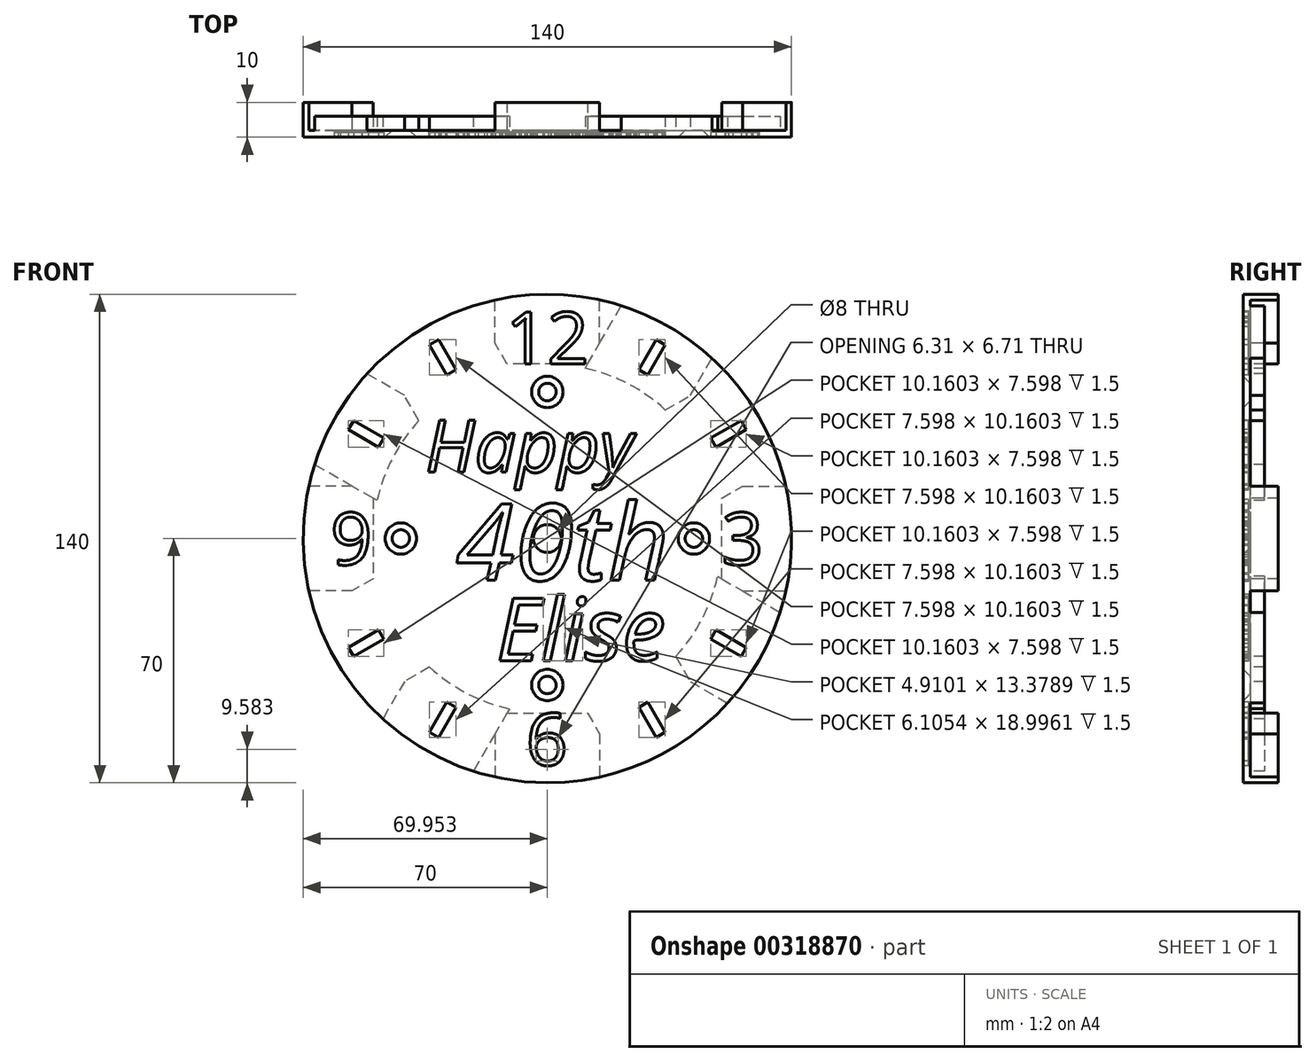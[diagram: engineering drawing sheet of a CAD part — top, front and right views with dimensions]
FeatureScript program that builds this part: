
annotation { "Feature Type Name" : "Feature", "Feature Type Description" : "" }
export const myFeature = defineFeature(function(context is Context, id is Id, definition is map)
    precondition{}
    {
        {
            var Q0;
            Q0=qCreatedBy(makeId("Front.planeOp"),FACE);
            var sketch = newSketch(context, id + "F0", { "sketchPlane" : qUnion([Q0])});
            skCircle(sketch, "E0", {"center": v(0, 0) * mm, "radius": 70 * mm});
            skCircle(sketch, "E1", {"center": v(0, 0) * mm, "radius": 50 * mm});
            skLineSegment(sketch, "E2", {"start": v(0, 50) * mm, "end": v(15, 50) * mm});
            skLineSegment(sketch, "E3.MirrorCS", {"start": v(0, 50) * mm, "end": v(-15, 50) * mm});
            skLineSegment(sketch, "E4", {"start": v(-15, 50) * mm, "end": v(-15, 87.34) * mm});
            skLineSegment(sketch, "E5.MirrorCS", {"start": v(15, 50) * mm, "end": v(15, 87.34) * mm});
            skCircle(sketch, "E6", {"center": v(0, 0) * mm, "radius": 30 * mm, "construction": true});
            skLineSegment(sketch, "E7", {"start": v(0, 0) * mm, "end": v(15, 25.98) * mm, "construction": true});
            skLineSegment(sketch, "E8", {"start": v(15, 25.98) * mm, "end": v(0, 0) * mm, "construction": true});
            skPoint(sketch, "E9.endSnap0", {"position": v(7.5, 13) * mm});
            skLineSegment(sketch, "E10", {"start": v(15, 25.98) * mm, "end": v(2, 33.48) * mm});
            skLineSegment(sketch, "E11.MirrorCS", {"start": v(15, 25.98) * mm, "end": v(28, 18.48) * mm});
            skLineSegment(sketch, "E12", {"start": v(2, 33.48) * mm, "end": v(34.2, 89.22) * mm});
            skLineSegment(sketch, "E13.MirrorCS", {"start": v(28, 18.48) * mm, "end": v(60.17, 74.22) * mm});
            skPoint(sketch, "E14.center", {"position": v(0, 10) * mm});
            skLineSegment(sketch, "E15", {"start": v(0, 0) * mm, "end": v(25.98, 15) * mm, "construction": true});
            skLineSegment(sketch, "E16", {"start": v(25.98, 15) * mm, "end": v(18.48, 28) * mm});
            skPoint(sketch, "E16.endSnap0", {"position": v(21.5, 22.23) * mm});
            skLineSegment(sketch, "E17", {"start": v(18.48, 28) * mm, "end": v(70.05, 57.76) * mm});
            skLineSegment(sketch, "E18.MirrorCS", {"start": v(25.98, 15) * mm, "end": v(33.48, 2) * mm});
            skLineSegment(sketch, "E19.MirrorCS", {"start": v(33.48, 2) * mm, "end": v(85.05, 31.78) * mm});
            skLineSegment(sketch, "E20.1.0", {"start": v(-50, -15) * mm, "end": v(-87.34, -15) * mm});
            skLineSegment(sketch, "E20.1.1", {"start": v(-50, 0) * mm, "end": v(-50, -15) * mm});
            skLineSegment(sketch, "E20.1.2", {"start": v(-50, 0) * mm, "end": v(-50, 15) * mm});
            skLineSegment(sketch, "E20.1.3", {"start": v(-50, 15) * mm, "end": v(-87.34, 15) * mm});
            skLineSegment(sketch, "E20.2.0", {"start": v(15, -50) * mm, "end": v(15, -87.34) * mm});
            skLineSegment(sketch, "E20.2.1", {"start": v(0, -50) * mm, "end": v(15, -50) * mm});
            skLineSegment(sketch, "E20.2.2", {"start": v(0, -50) * mm, "end": v(-15, -50) * mm});
            skLineSegment(sketch, "E20.2.3", {"start": v(-15, -50) * mm, "end": v(-15, -87.34) * mm});
            skLineSegment(sketch, "E20.3.0", {"start": v(50, 15) * mm, "end": v(87.34, 15) * mm});
            skLineSegment(sketch, "E20.3.1", {"start": v(50, 0) * mm, "end": v(50, 15) * mm});
            skLineSegment(sketch, "E20.3.2", {"start": v(50, 0) * mm, "end": v(50, -15) * mm});
            skLineSegment(sketch, "E20.3.3", {"start": v(50, -15) * mm, "end": v(87.34, -15) * mm});
            skLineSegment(sketch, "E21.1.0", {"start": v(-33.48, 2) * mm, "end": v(-89.22, 34.2) * mm});
            skLineSegment(sketch, "E21.1.1", {"start": v(-25.98, 15) * mm, "end": v(-33.48, 2) * mm});
            skLineSegment(sketch, "E21.1.2", {"start": v(-25.98, 15) * mm, "end": v(-18.48, 28) * mm});
            skLineSegment(sketch, "E21.1.3", {"start": v(-18.48, 28) * mm, "end": v(-74.22, 60.17) * mm});
            skLineSegment(sketch, "E21.2.0", {"start": v(-2, -33.48) * mm, "end": v(-34.2, -89.22) * mm});
            skLineSegment(sketch, "E21.2.1", {"start": v(-15, -25.98) * mm, "end": v(-2, -33.48) * mm});
            skLineSegment(sketch, "E21.2.2", {"start": v(-15, -25.98) * mm, "end": v(-28, -18.48) * mm});
            skLineSegment(sketch, "E21.2.3", {"start": v(-28, -18.48) * mm, "end": v(-60.17, -74.22) * mm});
            skLineSegment(sketch, "E21.3.0", {"start": v(33.48, -2) * mm, "end": v(89.22, -34.2) * mm});
            skLineSegment(sketch, "E21.3.1", {"start": v(25.98, -15) * mm, "end": v(33.48, -2) * mm});
            skLineSegment(sketch, "E21.3.2", {"start": v(25.98, -15) * mm, "end": v(18.48, -28) * mm});
            skLineSegment(sketch, "E21.3.3", {"start": v(18.48, -28) * mm, "end": v(74.22, -60.17) * mm});
            skLineSegment(sketch, "E22.1.0", {"start": v(-28, 18.48) * mm, "end": v(-57.76, 70.05) * mm});
            skLineSegment(sketch, "E22.1.1", {"start": v(-15, 25.98) * mm, "end": v(-28, 18.48) * mm});
            skLineSegment(sketch, "E22.1.2", {"start": v(-15, 25.98) * mm, "end": v(-2, 33.48) * mm});
            skLineSegment(sketch, "E22.1.3", {"start": v(-2, 33.48) * mm, "end": v(-31.78, 85.05) * mm});
            skLineSegment(sketch, "E22.2.0", {"start": v(-18.48, -28) * mm, "end": v(-70.05, -57.76) * mm});
            skLineSegment(sketch, "E22.2.1", {"start": v(-25.98, -15) * mm, "end": v(-18.48, -28) * mm});
            skLineSegment(sketch, "E22.2.2", {"start": v(-25.98, -15) * mm, "end": v(-33.48, -2) * mm});
            skLineSegment(sketch, "E22.2.3", {"start": v(-33.48, -2) * mm, "end": v(-85.05, -31.78) * mm});
            skLineSegment(sketch, "E22.3.0", {"start": v(28, -18.48) * mm, "end": v(57.76, -70.05) * mm});
            skLineSegment(sketch, "E22.3.1", {"start": v(15, -25.98) * mm, "end": v(28, -18.48) * mm});
            skLineSegment(sketch, "E22.3.2", {"start": v(15, -25.98) * mm, "end": v(2, -33.48) * mm});
            skLineSegment(sketch, "E22.3.3", {"start": v(2, -33.48) * mm, "end": v(31.78, -85.05) * mm});
            skCircle(sketch, "E23", {"center": v(0, 0) * mm, "radius": 4 * mm});
            skSolve(sketch);
        }
        {
            var Q0;
            {var subQ9=sQuery(id+"F0.wireOp",EDGE,"E10");Q0=makeQuery(id+"F0.imprint","IMPRINT",FACE,{"disambiguationData":[TD([[makeQuery(id+"F0.imprint","IMPRINT",EDGE,{"derivedFrom":subQ9}),1.0]])]});}
            var Q1;
            {var subQ0=sQuery(id+"F0.wireOp",EDGE,"E21.1.1");Q1=makeQuery(id+"F0.imprint","IMPRINT",FACE,{"disambiguationData":[TD([[makeQuery(id+"F0.imprint","IMPRINT",EDGE,{"derivedFrom":subQ0}),-1.0]])]});}
            var Q2;
            {var subQ6=sQuery(id+"F0.wireOp",EDGE,"E0");var subQ12=sQuery(id+"F0.wireOp",EDGE,"E21.1.3");var subQ13=makeQuery(id+"F0.imprint","INTERSECT",VERTEX,{"derivedFrom":[subQ6,subQ12]});Q2=makeQuery(id+"F0.imprint","IMPRINT",FACE,{"disambiguationData":[TD([[makeQuery(id+"F0.imprint","IMPRINT",EDGE,{"disambiguationData":[TD([[subQ13,-1.0]])],"derivedFrom":subQ6}),1.0]])]});}
            var Q3;
            {var subQ0=sQuery(id+"F0.wireOp",EDGE,"E21.1.0");var subQ1=sQuery(id+"F0.wireOp",EDGE,"E0");var subQ2=makeQuery(id+"F0.imprint","INTERSECT",VERTEX,{"derivedFrom":[subQ1,subQ0]});Q3=makeQuery(id+"F0.imprint","IMPRINT",FACE,{"disambiguationData":[TD([[makeQuery(id+"F0.imprint","IMPRINT",EDGE,{"disambiguationData":[TD([[subQ2,-1.0]])],"derivedFrom":subQ1}),1.0]])]});}
            var Q4;
            {var subQ1=sQuery(id+"F0.wireOp",EDGE,"E1");var subQ3=sQuery(id+"F0.wireOp",EDGE,"E21.1.0");var subQ4=makeQuery(id+"F0.imprint","INTERSECT",VERTEX,{"derivedFrom":[subQ1,subQ3]});Q4=makeQuery(id+"F0.imprint","IMPRINT",FACE,{"disambiguationData":[TD([[makeQuery(id+"F0.imprint","IMPRINT",EDGE,{"disambiguationData":[TD([[subQ4,-1.0]])],"derivedFrom":subQ3}),1.0]])]});}
            var Q5;
            {var subQ1=sQuery(id+"F0.wireOp",EDGE,"E1");var subQ3=sQuery(id+"F0.wireOp",EDGE,"E22.2.3");var subQ4=makeQuery(id+"F0.imprint","INTERSECT",VERTEX,{"derivedFrom":[subQ1,subQ3]});Q5=makeQuery(id+"F0.imprint","IMPRINT",FACE,{"disambiguationData":[TD([[makeQuery(id+"F0.imprint","IMPRINT",EDGE,{"disambiguationData":[TD([[subQ4,-1.0]])],"derivedFrom":subQ3}),-1.0]])]});}
            var Q6;
            {var subQ3=sQuery(id+"F0.wireOp",EDGE,"E22.2.3");var subQ6=sQuery(id+"F0.wireOp",EDGE,"E0");var subQ14=makeQuery(id+"F0.imprint","INTERSECT",VERTEX,{"derivedFrom":[subQ6,subQ3]});Q6=makeQuery(id+"F0.imprint","IMPRINT",FACE,{"disambiguationData":[TD([[makeQuery(id+"F0.imprint","IMPRINT",EDGE,{"disambiguationData":[TD([[subQ14,-1.0]])],"derivedFrom":subQ6}),1.0]])]});}
            var Q7;
            {var subQ0=sQuery(id+"F0.wireOp",EDGE,"E22.2.2");Q7=makeQuery(id+"F0.imprint","IMPRINT",FACE,{"disambiguationData":[TD([[makeQuery(id+"F0.imprint","IMPRINT",EDGE,{"derivedFrom":subQ0}),1.0]])]});}
            var Q8;
            {var subQ0=sQuery(id+"F0.wireOp",EDGE,"E20.1.0");var subQ1=sQuery(id+"F0.wireOp",EDGE,"E0");var subQ2=makeQuery(id+"F0.imprint","INTERSECT",VERTEX,{"derivedFrom":[subQ1,subQ0]});Q8=makeQuery(id+"F0.imprint","IMPRINT",FACE,{"disambiguationData":[TD([[makeQuery(id+"F0.imprint","IMPRINT",EDGE,{"disambiguationData":[TD([[subQ2,-1.0]])],"derivedFrom":subQ1}),1.0]])]});}
            var Q9;
            {var subQ0=sQuery(id+"F0.wireOp",EDGE,"E22.2.0");var subQ1=sQuery(id+"F0.wireOp",EDGE,"E0");var subQ2=makeQuery(id+"F0.imprint","INTERSECT",VERTEX,{"derivedFrom":[subQ1,subQ0]});Q9=makeQuery(id+"F0.imprint","IMPRINT",FACE,{"disambiguationData":[TD([[makeQuery(id+"F0.imprint","IMPRINT",EDGE,{"disambiguationData":[TD([[subQ2,-1.0]])],"derivedFrom":subQ1}),1.0]])]});}
            var Q10;
            {var subQ0=sQuery(id+"F0.wireOp",EDGE,"E21.2.0");var subQ1=sQuery(id+"F0.wireOp",EDGE,"E0");var subQ2=makeQuery(id+"F0.imprint","INTERSECT",VERTEX,{"derivedFrom":[subQ1,subQ0]});Q10=makeQuery(id+"F0.imprint","IMPRINT",FACE,{"disambiguationData":[TD([[makeQuery(id+"F0.imprint","IMPRINT",EDGE,{"disambiguationData":[TD([[subQ2,-1.0]])],"derivedFrom":subQ1}),1.0]])]});}
            var Q11;
            {var subQ0=sQuery(id+"F0.wireOp",EDGE,"E21.2.3");var subQ3=sQuery(id+"F0.wireOp",EDGE,"E1");var subQ4=makeQuery(id+"F0.imprint","INTERSECT",VERTEX,{"derivedFrom":[subQ3,subQ0]});Q11=makeQuery(id+"F0.imprint","IMPRINT",FACE,{"disambiguationData":[TD([[makeQuery(id+"F0.imprint","IMPRINT",EDGE,{"disambiguationData":[TD([[subQ4,-1.0]])],"derivedFrom":subQ3}),1.0]])]});}
            var Q12;
            {var subQ0=sQuery(id+"F0.wireOp",EDGE,"E21.2.1");Q12=makeQuery(id+"F0.imprint","IMPRINT",FACE,{"disambiguationData":[TD([[makeQuery(id+"F0.imprint","IMPRINT",EDGE,{"derivedFrom":subQ0}),-1.0]])]});}
            var Q13;
            {var subQ0=sQuery(id+"F0.wireOp",EDGE,"E21.2.3");var subQ1=sQuery(id+"F0.wireOp",EDGE,"E1");var subQ2=makeQuery(id+"F0.imprint","INTERSECT",VERTEX,{"derivedFrom":[subQ1,subQ0]});Q13=makeQuery(id+"F0.imprint","IMPRINT",FACE,{"disambiguationData":[TD([[makeQuery(id+"F0.imprint","IMPRINT",EDGE,{"disambiguationData":[TD([[subQ2,-1.0]])],"derivedFrom":subQ1}),-1.0]])]});}
            var Q14;
            {var subQ9=sQuery(id+"F0.wireOp",EDGE,"E21.2.3");var subQ10=sQuery(id+"F0.wireOp",EDGE,"E0");var subQ11=makeQuery(id+"F0.imprint","INTERSECT",VERTEX,{"derivedFrom":[subQ10,subQ9]});Q14=makeQuery(id+"F0.imprint","IMPRINT",FACE,{"disambiguationData":[TD([[makeQuery(id+"F0.imprint","IMPRINT",EDGE,{"disambiguationData":[TD([[subQ11,-1.0]])],"derivedFrom":subQ10}),1.0]])]});}
            var Q15;
            {var subQ1=sQuery(id+"F0.wireOp",EDGE,"E1");var subQ3=sQuery(id+"F0.wireOp",EDGE,"E21.2.0");var subQ4=makeQuery(id+"F0.imprint","INTERSECT",VERTEX,{"derivedFrom":[subQ1,subQ3]});Q15=makeQuery(id+"F0.imprint","IMPRINT",FACE,{"disambiguationData":[TD([[makeQuery(id+"F0.imprint","IMPRINT",EDGE,{"disambiguationData":[TD([[subQ4,-1.0]])],"derivedFrom":subQ3}),1.0]])]});}
            var Q16;
            {var subQ1=sQuery(id+"F0.wireOp",EDGE,"E1");var subQ3=sQuery(id+"F0.wireOp",EDGE,"E22.3.3");var subQ4=makeQuery(id+"F0.imprint","INTERSECT",VERTEX,{"derivedFrom":[subQ1,subQ3]});Q16=makeQuery(id+"F0.imprint","IMPRINT",FACE,{"disambiguationData":[TD([[makeQuery(id+"F0.imprint","IMPRINT",EDGE,{"disambiguationData":[TD([[subQ4,-1.0]])],"derivedFrom":subQ3}),-1.0]])]});}
            var Q17;
            {var subQ0=sQuery(id+"F0.wireOp",EDGE,"E20.2.0");var subQ1=sQuery(id+"F0.wireOp",EDGE,"E0");var subQ2=makeQuery(id+"F0.imprint","INTERSECT",VERTEX,{"derivedFrom":[subQ1,subQ0]});Q17=makeQuery(id+"F0.imprint","IMPRINT",FACE,{"disambiguationData":[TD([[makeQuery(id+"F0.imprint","IMPRINT",EDGE,{"disambiguationData":[TD([[subQ2,-1.0]])],"derivedFrom":subQ1}),1.0]])]});}
            var Q18;
            {var subQ0=sQuery(id+"F0.wireOp",EDGE,"E22.3.2");Q18=makeQuery(id+"F0.imprint","IMPRINT",FACE,{"disambiguationData":[TD([[makeQuery(id+"F0.imprint","IMPRINT",EDGE,{"derivedFrom":subQ0}),1.0]])]});}
            var Q19;
            {var subQ3=sQuery(id+"F0.wireOp",EDGE,"E22.3.3");var subQ12=sQuery(id+"F0.wireOp",EDGE,"E0");var subQ13=makeQuery(id+"F0.imprint","INTERSECT",VERTEX,{"derivedFrom":[subQ12,subQ3]});Q19=makeQuery(id+"F0.imprint","IMPRINT",FACE,{"disambiguationData":[TD([[makeQuery(id+"F0.imprint","IMPRINT",EDGE,{"disambiguationData":[TD([[subQ13,-1.0]])],"derivedFrom":subQ12}),1.0]])]});}
            var Q20;
            {var subQ0=sQuery(id+"F0.wireOp",EDGE,"E21.3.3");var subQ3=sQuery(id+"F0.wireOp",EDGE,"E1");var subQ4=makeQuery(id+"F0.imprint","INTERSECT",VERTEX,{"derivedFrom":[subQ3,subQ0]});Q20=makeQuery(id+"F0.imprint","IMPRINT",FACE,{"disambiguationData":[TD([[makeQuery(id+"F0.imprint","IMPRINT",EDGE,{"disambiguationData":[TD([[subQ4,-1.0]])],"derivedFrom":subQ3}),1.0]])]});}
            var Q21;
            {var subQ0=sQuery(id+"F0.wireOp",EDGE,"E21.3.1");Q21=makeQuery(id+"F0.imprint","IMPRINT",FACE,{"disambiguationData":[TD([[makeQuery(id+"F0.imprint","IMPRINT",EDGE,{"derivedFrom":subQ0}),-1.0]])]});}
            var Q22;
            {var subQ0=sQuery(id+"F0.wireOp",EDGE,"E21.3.3");var subQ1=sQuery(id+"F0.wireOp",EDGE,"E1");var subQ2=makeQuery(id+"F0.imprint","INTERSECT",VERTEX,{"derivedFrom":[subQ1,subQ0]});Q22=makeQuery(id+"F0.imprint","IMPRINT",FACE,{"disambiguationData":[TD([[makeQuery(id+"F0.imprint","IMPRINT",EDGE,{"disambiguationData":[TD([[subQ2,-1.0]])],"derivedFrom":subQ1}),-1.0]])]});}
            var Q23;
            {var subQ0=sQuery(id+"F0.wireOp",EDGE,"E22.3.0");var subQ1=sQuery(id+"F0.wireOp",EDGE,"E0");var subQ2=makeQuery(id+"F0.imprint","INTERSECT",VERTEX,{"derivedFrom":[subQ1,subQ0]});Q23=makeQuery(id+"F0.imprint","IMPRINT",FACE,{"disambiguationData":[TD([[makeQuery(id+"F0.imprint","IMPRINT",EDGE,{"disambiguationData":[TD([[subQ2,-1.0]])],"derivedFrom":subQ1}),1.0]])]});}
            var Q24;
            {var subQ10=sQuery(id+"F0.wireOp",EDGE,"E0");var subQ12=sQuery(id+"F0.wireOp",EDGE,"E21.3.3");var subQ13=makeQuery(id+"F0.imprint","INTERSECT",VERTEX,{"derivedFrom":[subQ10,subQ12]});Q24=makeQuery(id+"F0.imprint","IMPRINT",FACE,{"disambiguationData":[TD([[makeQuery(id+"F0.imprint","IMPRINT",EDGE,{"disambiguationData":[TD([[subQ13,-1.0]])],"derivedFrom":subQ10}),1.0]])]});}
            var Q25;
            {var subQ1=sQuery(id+"F0.wireOp",EDGE,"E1");var subQ3=sQuery(id+"F0.wireOp",EDGE,"E21.3.0");var subQ4=makeQuery(id+"F0.imprint","INTERSECT",VERTEX,{"derivedFrom":[subQ1,subQ3]});Q25=makeQuery(id+"F0.imprint","IMPRINT",FACE,{"disambiguationData":[TD([[makeQuery(id+"F0.imprint","IMPRINT",EDGE,{"disambiguationData":[TD([[subQ4,-1.0]])],"derivedFrom":subQ3}),1.0]])]});}
            var Q26;
            {var subQ1=sQuery(id+"F0.wireOp",EDGE,"E1");var subQ3=sQuery(id+"F0.wireOp",EDGE,"E19.MirrorCS");var subQ4=makeQuery(id+"F0.imprint","INTERSECT",VERTEX,{"derivedFrom":[subQ1,subQ3]});Q26=makeQuery(id+"F0.imprint","IMPRINT",FACE,{"disambiguationData":[TD([[makeQuery(id+"F0.imprint","IMPRINT",EDGE,{"disambiguationData":[TD([[subQ4,-1.0]])],"derivedFrom":subQ3}),-1.0]])]});}
            var Q27;
            {var subQ0=sQuery(id+"F0.wireOp",EDGE,"E18.MirrorCS");Q27=makeQuery(id+"F0.imprint","IMPRINT",FACE,{"disambiguationData":[TD([[makeQuery(id+"F0.imprint","IMPRINT",EDGE,{"derivedFrom":subQ0}),1.0]])]});}
            var Q28;
            {var subQ5=sQuery(id+"F0.wireOp",EDGE,"E19.MirrorCS");var subQ6=sQuery(id+"F0.wireOp",EDGE,"E0");var subQ7=makeQuery(id+"F0.imprint","INTERSECT",VERTEX,{"derivedFrom":[subQ6,subQ5]});Q28=makeQuery(id+"F0.imprint","IMPRINT",FACE,{"disambiguationData":[TD([[makeQuery(id+"F0.imprint","IMPRINT",EDGE,{"disambiguationData":[TD([[subQ7,-1.0]])],"derivedFrom":subQ6}),1.0]])]});}
            var Q29;
            {var subQ0=sQuery(id+"F0.wireOp",EDGE,"E19.MirrorCS");var subQ1=sQuery(id+"F0.wireOp",EDGE,"E0");var subQ2=makeQuery(id+"F0.imprint","INTERSECT",VERTEX,{"derivedFrom":[subQ1,subQ0]});Q29=makeQuery(id+"F0.imprint","IMPRINT",FACE,{"disambiguationData":[TD([[makeQuery(id+"F0.imprint","IMPRINT",EDGE,{"disambiguationData":[TD([[subQ2,1.0]])],"derivedFrom":subQ1}),1.0]])]});}
            var Q30;
            {var subQ5=sQuery(id+"F0.wireOp",EDGE,"E13.MirrorCS");var subQ7=sQuery(id+"F0.wireOp",EDGE,"E1");var subQ8=makeQuery(id+"F0.imprint","INTERSECT",VERTEX,{"derivedFrom":[subQ7,subQ5]});Q30=makeQuery(id+"F0.imprint","IMPRINT",FACE,{"disambiguationData":[TD([[makeQuery(id+"F0.imprint","IMPRINT",EDGE,{"disambiguationData":[TD([[subQ8,-1.0]])],"derivedFrom":subQ7}),1.0]])]});}
            var Q31;
            {var subQ1=sQuery(id+"F0.wireOp",EDGE,"E10");Q31=makeQuery(id+"F0.imprint","IMPRINT",FACE,{"disambiguationData":[TD([[makeQuery(id+"F0.imprint","IMPRINT",EDGE,{"derivedFrom":subQ1}),-1.0]])]});}
            var Q32;
            {var subQ0=sQuery(id+"F0.wireOp",EDGE,"E13.MirrorCS");var subQ1=sQuery(id+"F0.wireOp",EDGE,"E1");var subQ2=makeQuery(id+"F0.imprint","INTERSECT",VERTEX,{"derivedFrom":[subQ1,subQ0]});Q32=makeQuery(id+"F0.imprint","IMPRINT",FACE,{"disambiguationData":[TD([[makeQuery(id+"F0.imprint","IMPRINT",EDGE,{"disambiguationData":[TD([[subQ2,-1.0]])],"derivedFrom":subQ1}),-1.0]])]});}
            var Q33;
            {var subQ5=sQuery(id+"F0.wireOp",EDGE,"E13.MirrorCS");var subQ6=sQuery(id+"F0.wireOp",EDGE,"E0");var subQ7=makeQuery(id+"F0.imprint","INTERSECT",VERTEX,{"derivedFrom":[subQ6,subQ5]});Q33=makeQuery(id+"F0.imprint","IMPRINT",FACE,{"disambiguationData":[TD([[makeQuery(id+"F0.imprint","IMPRINT",EDGE,{"disambiguationData":[TD([[subQ7,-1.0]])],"derivedFrom":subQ6}),1.0]])]});}
            var Q34;
            {var subQ0=sQuery(id+"F0.wireOp",EDGE,"E17");var subQ1=sQuery(id+"F0.wireOp",EDGE,"E0");var subQ2=makeQuery(id+"F0.imprint","INTERSECT",VERTEX,{"derivedFrom":[subQ1,subQ0]});Q34=makeQuery(id+"F0.imprint","IMPRINT",FACE,{"disambiguationData":[TD([[makeQuery(id+"F0.imprint","IMPRINT",EDGE,{"disambiguationData":[TD([[subQ2,-1.0]])],"derivedFrom":subQ1}),1.0]])]});}
            var Q35;
            {var subQ0=sQuery(id+"F0.wireOp",EDGE,"E12");var subQ1=sQuery(id+"F0.wireOp",EDGE,"E0");var subQ2=makeQuery(id+"F0.imprint","INTERSECT",VERTEX,{"derivedFrom":[subQ1,subQ0]});Q35=makeQuery(id+"F0.imprint","IMPRINT",FACE,{"disambiguationData":[TD([[makeQuery(id+"F0.imprint","IMPRINT",EDGE,{"disambiguationData":[TD([[subQ2,-1.0]])],"derivedFrom":subQ1}),1.0]])]});}
            var Q36;
            {var subQ1=sQuery(id+"F0.wireOp",EDGE,"E1");var subQ3=sQuery(id+"F0.wireOp",EDGE,"E12");var subQ4=makeQuery(id+"F0.imprint","INTERSECT",VERTEX,{"derivedFrom":[subQ1,subQ3]});Q36=makeQuery(id+"F0.imprint","IMPRINT",FACE,{"disambiguationData":[TD([[makeQuery(id+"F0.imprint","IMPRINT",EDGE,{"disambiguationData":[TD([[subQ4,-1.0]])],"derivedFrom":subQ3}),1.0]])]});}
            var Q37;
            {var subQ1=sQuery(id+"F0.wireOp",EDGE,"E1");var subQ3=sQuery(id+"F0.wireOp",EDGE,"E22.1.3");var subQ4=makeQuery(id+"F0.imprint","INTERSECT",VERTEX,{"derivedFrom":[subQ1,subQ3]});Q37=makeQuery(id+"F0.imprint","IMPRINT",FACE,{"disambiguationData":[TD([[makeQuery(id+"F0.imprint","IMPRINT",EDGE,{"disambiguationData":[TD([[subQ4,-1.0]])],"derivedFrom":subQ3}),-1.0]])]});}
            var Q38;
            {var subQ0=sQuery(id+"F0.wireOp",EDGE,"E22.1.2");Q38=makeQuery(id+"F0.imprint","IMPRINT",FACE,{"disambiguationData":[TD([[makeQuery(id+"F0.imprint","IMPRINT",EDGE,{"derivedFrom":subQ0}),1.0]])]});}
            var Q39;
            {var subQ0=sQuery(id+"F0.wireOp",EDGE,"E21.1.3");var subQ3=sQuery(id+"F0.wireOp",EDGE,"E1");var subQ4=makeQuery(id+"F0.imprint","INTERSECT",VERTEX,{"derivedFrom":[subQ3,subQ0]});Q39=makeQuery(id+"F0.imprint","IMPRINT",FACE,{"disambiguationData":[TD([[makeQuery(id+"F0.imprint","IMPRINT",EDGE,{"disambiguationData":[TD([[subQ4,-1.0]])],"derivedFrom":subQ3}),1.0]])]});}
            var Q40;
            {var subQ0=sQuery(id+"F0.wireOp",EDGE,"E21.1.3");var subQ1=sQuery(id+"F0.wireOp",EDGE,"E1");var subQ2=makeQuery(id+"F0.imprint","INTERSECT",VERTEX,{"derivedFrom":[subQ1,subQ0]});Q40=makeQuery(id+"F0.imprint","IMPRINT",FACE,{"disambiguationData":[TD([[makeQuery(id+"F0.imprint","IMPRINT",EDGE,{"disambiguationData":[TD([[subQ2,-1.0]])],"derivedFrom":subQ1}),-1.0]])]});}
            var Q41;
            {var subQ0=sQuery(id+"F0.wireOp",EDGE,"E22.1.0");var subQ1=sQuery(id+"F0.wireOp",EDGE,"E0");var subQ2=makeQuery(id+"F0.imprint","INTERSECT",VERTEX,{"derivedFrom":[subQ1,subQ0]});Q41=makeQuery(id+"F0.imprint","IMPRINT",FACE,{"disambiguationData":[TD([[makeQuery(id+"F0.imprint","IMPRINT",EDGE,{"disambiguationData":[TD([[subQ2,-1.0]])],"derivedFrom":subQ1}),1.0]])]});}
            var Q42;
            {var subQ3=sQuery(id+"F0.wireOp",EDGE,"E22.1.3");var subQ10=sQuery(id+"F0.wireOp",EDGE,"E0");var subQ11=makeQuery(id+"F0.imprint","INTERSECT",VERTEX,{"derivedFrom":[subQ10,subQ3]});Q42=makeQuery(id+"F0.imprint","IMPRINT",FACE,{"disambiguationData":[TD([[makeQuery(id+"F0.imprint","IMPRINT",EDGE,{"disambiguationData":[TD([[subQ11,-1.0]])],"derivedFrom":subQ10}),1.0]])]});}
            var Q43;
            {var subQ0=sQuery(id+"F0.wireOp",EDGE,"E4");var subQ1=sQuery(id+"F0.wireOp",EDGE,"E0");var subQ2=makeQuery(id+"F0.imprint","INTERSECT",VERTEX,{"derivedFrom":[subQ1,subQ0]});Q43=makeQuery(id+"F0.imprint","IMPRINT",FACE,{"disambiguationData":[TD([[makeQuery(id+"F0.imprint","IMPRINT",EDGE,{"disambiguationData":[TD([[subQ2,-1.0]])],"derivedFrom":subQ1}),1.0]])]});}
            var Q44;
            {var subQ0=sQuery(id+"F0.wireOp",EDGE,"E21.3.0");var subQ1=sQuery(id+"F0.wireOp",EDGE,"E0");var subQ2=makeQuery(id+"F0.imprint","INTERSECT",VERTEX,{"derivedFrom":[subQ1,subQ0]});Q44=makeQuery(id+"F0.imprint","IMPRINT",FACE,{"disambiguationData":[TD([[makeQuery(id+"F0.imprint","IMPRINT",EDGE,{"disambiguationData":[TD([[subQ2,-1.0]])],"derivedFrom":subQ1}),1.0]])]});}
            var Q45;
            {var subQ0=sQuery(id+"F0.wireOp",EDGE,"E4");var subQ1=sQuery(id+"F0.wireOp",EDGE,"E3.MirrorCS");var subQ2=makeQuery(id+"F0.imprint","INTERSECT",VERTEX,{"derivedFrom":[subQ1,subQ0]});Q45=makeQuery(id+"F0.imprint","IMPRINT",FACE,{"disambiguationData":[TD([[makeQuery(id+"F0.imprint","IMPRINT",EDGE,{"disambiguationData":[TD([[subQ2,1.0]])],"derivedFrom":subQ1}),-1.0]])]});}
            var Q46;
            {var subQ7=sQuery(id+"F0.wireOp",EDGE,"E5.MirrorCS");var subQ11=sQuery(id+"F0.wireOp",EDGE,"E0");var subQ13=makeQuery(id+"F0.imprint","INTERSECT",VERTEX,{"derivedFrom":[subQ11,subQ7]});Q46=makeQuery(id+"F0.imprint","IMPRINT",FACE,{"disambiguationData":[TD([[makeQuery(id+"F0.imprint","IMPRINT",EDGE,{"disambiguationData":[TD([[subQ13,-1.0]])],"derivedFrom":subQ11}),1.0]])]});}
            var Q47;
            {var subQ0=sQuery(id+"F0.wireOp",EDGE,"E5.MirrorCS");var subQ1=sQuery(id+"F0.wireOp",EDGE,"E2");var subQ2=makeQuery(id+"F0.imprint","INTERSECT",VERTEX,{"derivedFrom":[subQ1,subQ0]});Q47=makeQuery(id+"F0.imprint","IMPRINT",FACE,{"disambiguationData":[TD([[makeQuery(id+"F0.imprint","IMPRINT",EDGE,{"disambiguationData":[TD([[subQ2,1.0]])],"derivedFrom":subQ1}),1.0]])]});}
            var Q48;
            {var subQ6=sQuery(id+"F0.wireOp",EDGE,"E0");var subQ11=sQuery(id+"F0.wireOp",EDGE,"E20.1.3");var subQ13=makeQuery(id+"F0.imprint","INTERSECT",VERTEX,{"derivedFrom":[subQ6,subQ11]});Q48=makeQuery(id+"F0.imprint","IMPRINT",FACE,{"disambiguationData":[TD([[makeQuery(id+"F0.imprint","IMPRINT",EDGE,{"disambiguationData":[TD([[subQ13,-1.0]])],"derivedFrom":subQ6}),1.0]])]});}
            var Q49;
            {var subQ0=sQuery(id+"F0.wireOp",EDGE,"E20.1.3");var subQ1=sQuery(id+"F0.wireOp",EDGE,"E20.1.2");var subQ2=makeQuery(id+"F0.imprint","INTERSECT",VERTEX,{"derivedFrom":[subQ1,subQ0]});Q49=makeQuery(id+"F0.imprint","IMPRINT",FACE,{"disambiguationData":[TD([[makeQuery(id+"F0.imprint","IMPRINT",EDGE,{"disambiguationData":[TD([[subQ2,1.0]])],"derivedFrom":subQ1}),1.0]])]});}
            var Q50;
            {var subQ0=sQuery(id+"F0.wireOp",EDGE,"E20.1.1");var subQ1=sQuery(id+"F0.wireOp",EDGE,"E20.1.0");var subQ2=makeQuery(id+"F0.imprint","INTERSECT",VERTEX,{"derivedFrom":[subQ1,subQ0]});Q50=makeQuery(id+"F0.imprint","IMPRINT",FACE,{"disambiguationData":[TD([[makeQuery(id+"F0.imprint","IMPRINT",EDGE,{"disambiguationData":[TD([[subQ2,-1.0]])],"derivedFrom":subQ1}),-1.0]])]});}
            var Q51;
            {var subQ6=sQuery(id+"F0.wireOp",EDGE,"E0");var subQ11=sQuery(id+"F0.wireOp",EDGE,"E20.2.3");var subQ12=makeQuery(id+"F0.imprint","INTERSECT",VERTEX,{"derivedFrom":[subQ6,subQ11]});Q51=makeQuery(id+"F0.imprint","IMPRINT",FACE,{"disambiguationData":[TD([[makeQuery(id+"F0.imprint","IMPRINT",EDGE,{"disambiguationData":[TD([[subQ12,-1.0]])],"derivedFrom":subQ6}),1.0]])]});}
            var Q52;
            {var subQ0=sQuery(id+"F0.wireOp",EDGE,"E20.2.3");var subQ1=sQuery(id+"F0.wireOp",EDGE,"E20.2.2");var subQ2=makeQuery(id+"F0.imprint","INTERSECT",VERTEX,{"derivedFrom":[subQ1,subQ0]});Q52=makeQuery(id+"F0.imprint","IMPRINT",FACE,{"disambiguationData":[TD([[makeQuery(id+"F0.imprint","IMPRINT",EDGE,{"disambiguationData":[TD([[subQ2,1.0]])],"derivedFrom":subQ1}),1.0]])]});}
            var Q53;
            {var subQ0=sQuery(id+"F0.wireOp",EDGE,"E20.2.1");var subQ1=sQuery(id+"F0.wireOp",EDGE,"E20.2.0");var subQ2=makeQuery(id+"F0.imprint","INTERSECT",VERTEX,{"derivedFrom":[subQ1,subQ0]});Q53=makeQuery(id+"F0.imprint","IMPRINT",FACE,{"disambiguationData":[TD([[makeQuery(id+"F0.imprint","IMPRINT",EDGE,{"disambiguationData":[TD([[subQ2,-1.0]])],"derivedFrom":subQ1}),-1.0]])]});}
            var Q54;
            {var subQ0=sQuery(id+"F0.wireOp",EDGE,"E20.3.3");var subQ1=sQuery(id+"F0.wireOp",EDGE,"E20.3.2");var subQ2=makeQuery(id+"F0.imprint","INTERSECT",VERTEX,{"derivedFrom":[subQ1,subQ0]});Q54=makeQuery(id+"F0.imprint","IMPRINT",FACE,{"disambiguationData":[TD([[makeQuery(id+"F0.imprint","IMPRINT",EDGE,{"disambiguationData":[TD([[subQ2,1.0]])],"derivedFrom":subQ1}),1.0]])]});}
            var Q55;
            {var subQ0=sQuery(id+"F0.wireOp",EDGE,"E20.3.0");var subQ1=sQuery(id+"F0.wireOp",EDGE,"E0");var subQ2=makeQuery(id+"F0.imprint","INTERSECT",VERTEX,{"derivedFrom":[subQ1,subQ0]});Q55=makeQuery(id+"F0.imprint","IMPRINT",FACE,{"disambiguationData":[TD([[makeQuery(id+"F0.imprint","IMPRINT",EDGE,{"disambiguationData":[TD([[subQ2,1.0]])],"derivedFrom":subQ1}),1.0]])]});}
            var Q56;
            {var subQ0=sQuery(id+"F0.wireOp",EDGE,"E20.3.1");var subQ1=sQuery(id+"F0.wireOp",EDGE,"E19.MirrorCS");var subQ2=makeQuery(id+"F0.imprint","INTERSECT",VERTEX,{"derivedFrom":[subQ1,subQ0]});Q56=makeQuery(id+"F0.imprint","IMPRINT",FACE,{"disambiguationData":[TD([[makeQuery(id+"F0.imprint","IMPRINT",EDGE,{"disambiguationData":[TD([[subQ2,-1.0]])],"derivedFrom":subQ1}),1.0]])]});}
            extrude(context, id + "F1", {"entities" : qUnion([Q0, Q1, Q2, Q3, Q4, Q5, Q6, Q7, Q8, Q9, Q10, Q11, Q12, Q13, Q14, Q15, Q16, Q17, Q18, Q19, Q20, Q21, Q22, Q23, Q24, Q25, Q26, Q27, Q28, Q29, Q30, Q31, Q32, Q33, Q34, Q35, Q36, Q37, Q38, Q39, Q40, Q41, Q42, Q43, Q44, Q45, Q46, Q47, Q48, Q49, Q50, Q51, Q52, Q53, Q54, Q55, Q56]), "depth" : 8 * mm});
        }
        {
            var Q0;
            {var subQ0=sQuery(id+"F0.wireOp",EDGE,"E19.MirrorCS");var subQ1=sQuery(id+"F0.wireOp",EDGE,"E0");var subQ2=makeQuery(id+"F0.imprint","INTERSECT",VERTEX,{"derivedFrom":[subQ1,subQ0]});Q0=makeQuery(id+"F0.imprint","IMPRINT",FACE,{"disambiguationData":[TD([[makeQuery(id+"F0.imprint","IMPRINT",EDGE,{"disambiguationData":[TD([[subQ2,1.0]])],"derivedFrom":subQ1}),1.0]])]});}
            var Q1;
            {var subQ0=sQuery(id+"F0.wireOp",EDGE,"E20.3.0");var subQ1=sQuery(id+"F0.wireOp",EDGE,"E0");var subQ2=makeQuery(id+"F0.imprint","INTERSECT",VERTEX,{"derivedFrom":[subQ1,subQ0]});Q1=makeQuery(id+"F0.imprint","IMPRINT",FACE,{"disambiguationData":[TD([[makeQuery(id+"F0.imprint","IMPRINT",EDGE,{"disambiguationData":[TD([[subQ2,1.0]])],"derivedFrom":subQ1}),1.0]])]});}
            var Q2;
            {var subQ9=sQuery(id+"F0.wireOp",EDGE,"E10");Q2=makeQuery(id+"F0.imprint","IMPRINT",FACE,{"disambiguationData":[TD([[makeQuery(id+"F0.imprint","IMPRINT",EDGE,{"derivedFrom":subQ9}),1.0]])]});}
            var Q3;
            {var subQ1=sQuery(id+"F0.wireOp",EDGE,"E1");var subQ3=sQuery(id+"F0.wireOp",EDGE,"E19.MirrorCS");var subQ4=makeQuery(id+"F0.imprint","INTERSECT",VERTEX,{"derivedFrom":[subQ1,subQ3]});Q3=makeQuery(id+"F0.imprint","IMPRINT",FACE,{"disambiguationData":[TD([[makeQuery(id+"F0.imprint","IMPRINT",EDGE,{"disambiguationData":[TD([[subQ4,-1.0]])],"derivedFrom":subQ3}),-1.0]])]});}
            var Q4;
            {var subQ1=sQuery(id+"F0.wireOp",EDGE,"E1");var subQ3=sQuery(id+"F0.wireOp",EDGE,"E21.3.0");var subQ4=makeQuery(id+"F0.imprint","INTERSECT",VERTEX,{"derivedFrom":[subQ1,subQ3]});Q4=makeQuery(id+"F0.imprint","IMPRINT",FACE,{"disambiguationData":[TD([[makeQuery(id+"F0.imprint","IMPRINT",EDGE,{"disambiguationData":[TD([[subQ4,-1.0]])],"derivedFrom":subQ3}),1.0]])]});}
            var Q5;
            {var subQ1=sQuery(id+"F0.wireOp",EDGE,"E1");var subQ3=sQuery(id+"F0.wireOp",EDGE,"E12");var subQ4=makeQuery(id+"F0.imprint","INTERSECT",VERTEX,{"derivedFrom":[subQ1,subQ3]});Q5=makeQuery(id+"F0.imprint","IMPRINT",FACE,{"disambiguationData":[TD([[makeQuery(id+"F0.imprint","IMPRINT",EDGE,{"disambiguationData":[TD([[subQ4,-1.0]])],"derivedFrom":subQ3}),1.0]])]});}
            var Q6;
            {var subQ1=sQuery(id+"F0.wireOp",EDGE,"E1");var subQ3=sQuery(id+"F0.wireOp",EDGE,"E22.1.3");var subQ4=makeQuery(id+"F0.imprint","INTERSECT",VERTEX,{"derivedFrom":[subQ1,subQ3]});Q6=makeQuery(id+"F0.imprint","IMPRINT",FACE,{"disambiguationData":[TD([[makeQuery(id+"F0.imprint","IMPRINT",EDGE,{"disambiguationData":[TD([[subQ4,-1.0]])],"derivedFrom":subQ3}),-1.0]])]});}
            var Q7;
            {var subQ7=sQuery(id+"F0.wireOp",EDGE,"E5.MirrorCS");var subQ11=sQuery(id+"F0.wireOp",EDGE,"E0");var subQ13=makeQuery(id+"F0.imprint","INTERSECT",VERTEX,{"derivedFrom":[subQ11,subQ7]});Q7=makeQuery(id+"F0.imprint","IMPRINT",FACE,{"disambiguationData":[TD([[makeQuery(id+"F0.imprint","IMPRINT",EDGE,{"disambiguationData":[TD([[subQ13,-1.0]])],"derivedFrom":subQ11}),1.0]])]});}
            var Q8;
            {var subQ0=sQuery(id+"F0.wireOp",EDGE,"E12");var subQ1=sQuery(id+"F0.wireOp",EDGE,"E0");var subQ2=makeQuery(id+"F0.imprint","INTERSECT",VERTEX,{"derivedFrom":[subQ1,subQ0]});Q8=makeQuery(id+"F0.imprint","IMPRINT",FACE,{"disambiguationData":[TD([[makeQuery(id+"F0.imprint","IMPRINT",EDGE,{"disambiguationData":[TD([[subQ2,-1.0]])],"derivedFrom":subQ1}),1.0]])]});}
            var Q9;
            {var subQ0=sQuery(id+"F0.wireOp",EDGE,"E17");var subQ1=sQuery(id+"F0.wireOp",EDGE,"E0");var subQ2=makeQuery(id+"F0.imprint","INTERSECT",VERTEX,{"derivedFrom":[subQ1,subQ0]});Q9=makeQuery(id+"F0.imprint","IMPRINT",FACE,{"disambiguationData":[TD([[makeQuery(id+"F0.imprint","IMPRINT",EDGE,{"disambiguationData":[TD([[subQ2,-1.0]])],"derivedFrom":subQ1}),1.0]])]});}
            var Q10;
            {var subQ0=sQuery(id+"F0.wireOp",EDGE,"E4");var subQ1=sQuery(id+"F0.wireOp",EDGE,"E0");var subQ2=makeQuery(id+"F0.imprint","INTERSECT",VERTEX,{"derivedFrom":[subQ1,subQ0]});Q10=makeQuery(id+"F0.imprint","IMPRINT",FACE,{"disambiguationData":[TD([[makeQuery(id+"F0.imprint","IMPRINT",EDGE,{"disambiguationData":[TD([[subQ2,-1.0]])],"derivedFrom":subQ1}),1.0]])]});}
            var Q11;
            {var subQ0=sQuery(id+"F0.wireOp",EDGE,"E22.1.0");var subQ1=sQuery(id+"F0.wireOp",EDGE,"E0");var subQ2=makeQuery(id+"F0.imprint","INTERSECT",VERTEX,{"derivedFrom":[subQ1,subQ0]});Q11=makeQuery(id+"F0.imprint","IMPRINT",FACE,{"disambiguationData":[TD([[makeQuery(id+"F0.imprint","IMPRINT",EDGE,{"disambiguationData":[TD([[subQ2,-1.0]])],"derivedFrom":subQ1}),1.0]])]});}
            var Q12;
            {var subQ0=sQuery(id+"F0.wireOp",EDGE,"E21.1.0");var subQ1=sQuery(id+"F0.wireOp",EDGE,"E0");var subQ2=makeQuery(id+"F0.imprint","INTERSECT",VERTEX,{"derivedFrom":[subQ1,subQ0]});Q12=makeQuery(id+"F0.imprint","IMPRINT",FACE,{"disambiguationData":[TD([[makeQuery(id+"F0.imprint","IMPRINT",EDGE,{"disambiguationData":[TD([[subQ2,-1.0]])],"derivedFrom":subQ1}),1.0]])]});}
            var Q13;
            {var subQ1=sQuery(id+"F0.wireOp",EDGE,"E1");var subQ3=sQuery(id+"F0.wireOp",EDGE,"E21.1.0");var subQ4=makeQuery(id+"F0.imprint","INTERSECT",VERTEX,{"derivedFrom":[subQ1,subQ3]});Q13=makeQuery(id+"F0.imprint","IMPRINT",FACE,{"disambiguationData":[TD([[makeQuery(id+"F0.imprint","IMPRINT",EDGE,{"disambiguationData":[TD([[subQ4,-1.0]])],"derivedFrom":subQ3}),1.0]])]});}
            var Q14;
            {var subQ1=sQuery(id+"F0.wireOp",EDGE,"E1");var subQ3=sQuery(id+"F0.wireOp",EDGE,"E22.2.3");var subQ4=makeQuery(id+"F0.imprint","INTERSECT",VERTEX,{"derivedFrom":[subQ1,subQ3]});Q14=makeQuery(id+"F0.imprint","IMPRINT",FACE,{"disambiguationData":[TD([[makeQuery(id+"F0.imprint","IMPRINT",EDGE,{"disambiguationData":[TD([[subQ4,-1.0]])],"derivedFrom":subQ3}),-1.0]])]});}
            var Q15;
            {var subQ6=sQuery(id+"F0.wireOp",EDGE,"E0");var subQ11=sQuery(id+"F0.wireOp",EDGE,"E20.1.3");var subQ13=makeQuery(id+"F0.imprint","INTERSECT",VERTEX,{"derivedFrom":[subQ6,subQ11]});Q15=makeQuery(id+"F0.imprint","IMPRINT",FACE,{"disambiguationData":[TD([[makeQuery(id+"F0.imprint","IMPRINT",EDGE,{"disambiguationData":[TD([[subQ13,-1.0]])],"derivedFrom":subQ6}),1.0]])]});}
            var Q16;
            {var subQ0=sQuery(id+"F0.wireOp",EDGE,"E20.1.0");var subQ1=sQuery(id+"F0.wireOp",EDGE,"E0");var subQ2=makeQuery(id+"F0.imprint","INTERSECT",VERTEX,{"derivedFrom":[subQ1,subQ0]});Q16=makeQuery(id+"F0.imprint","IMPRINT",FACE,{"disambiguationData":[TD([[makeQuery(id+"F0.imprint","IMPRINT",EDGE,{"disambiguationData":[TD([[subQ2,-1.0]])],"derivedFrom":subQ1}),1.0]])]});}
            var Q17;
            {var subQ0=sQuery(id+"F0.wireOp",EDGE,"E21.3.0");var subQ1=sQuery(id+"F0.wireOp",EDGE,"E0");var subQ2=makeQuery(id+"F0.imprint","INTERSECT",VERTEX,{"derivedFrom":[subQ1,subQ0]});Q17=makeQuery(id+"F0.imprint","IMPRINT",FACE,{"disambiguationData":[TD([[makeQuery(id+"F0.imprint","IMPRINT",EDGE,{"disambiguationData":[TD([[subQ2,-1.0]])],"derivedFrom":subQ1}),1.0]])]});}
            var Q18;
            {var subQ0=sQuery(id+"F0.wireOp",EDGE,"E22.3.0");var subQ1=sQuery(id+"F0.wireOp",EDGE,"E0");var subQ2=makeQuery(id+"F0.imprint","INTERSECT",VERTEX,{"derivedFrom":[subQ1,subQ0]});Q18=makeQuery(id+"F0.imprint","IMPRINT",FACE,{"disambiguationData":[TD([[makeQuery(id+"F0.imprint","IMPRINT",EDGE,{"disambiguationData":[TD([[subQ2,-1.0]])],"derivedFrom":subQ1}),1.0]])]});}
            var Q19;
            {var subQ0=sQuery(id+"F0.wireOp",EDGE,"E20.2.0");var subQ1=sQuery(id+"F0.wireOp",EDGE,"E0");var subQ2=makeQuery(id+"F0.imprint","INTERSECT",VERTEX,{"derivedFrom":[subQ1,subQ0]});Q19=makeQuery(id+"F0.imprint","IMPRINT",FACE,{"disambiguationData":[TD([[makeQuery(id+"F0.imprint","IMPRINT",EDGE,{"disambiguationData":[TD([[subQ2,-1.0]])],"derivedFrom":subQ1}),1.0]])]});}
            var Q20;
            {var subQ6=sQuery(id+"F0.wireOp",EDGE,"E0");var subQ11=sQuery(id+"F0.wireOp",EDGE,"E20.2.3");var subQ12=makeQuery(id+"F0.imprint","INTERSECT",VERTEX,{"derivedFrom":[subQ6,subQ11]});Q20=makeQuery(id+"F0.imprint","IMPRINT",FACE,{"disambiguationData":[TD([[makeQuery(id+"F0.imprint","IMPRINT",EDGE,{"disambiguationData":[TD([[subQ12,-1.0]])],"derivedFrom":subQ6}),1.0]])]});}
            var Q21;
            {var subQ1=sQuery(id+"F0.wireOp",EDGE,"E1");var subQ3=sQuery(id+"F0.wireOp",EDGE,"E22.3.3");var subQ4=makeQuery(id+"F0.imprint","INTERSECT",VERTEX,{"derivedFrom":[subQ1,subQ3]});Q21=makeQuery(id+"F0.imprint","IMPRINT",FACE,{"disambiguationData":[TD([[makeQuery(id+"F0.imprint","IMPRINT",EDGE,{"disambiguationData":[TD([[subQ4,-1.0]])],"derivedFrom":subQ3}),-1.0]])]});}
            var Q22;
            {var subQ1=sQuery(id+"F0.wireOp",EDGE,"E1");var subQ3=sQuery(id+"F0.wireOp",EDGE,"E21.2.0");var subQ4=makeQuery(id+"F0.imprint","INTERSECT",VERTEX,{"derivedFrom":[subQ1,subQ3]});Q22=makeQuery(id+"F0.imprint","IMPRINT",FACE,{"disambiguationData":[TD([[makeQuery(id+"F0.imprint","IMPRINT",EDGE,{"disambiguationData":[TD([[subQ4,-1.0]])],"derivedFrom":subQ3}),1.0]])]});}
            var Q23;
            {var subQ0=sQuery(id+"F0.wireOp",EDGE,"E21.2.0");var subQ1=sQuery(id+"F0.wireOp",EDGE,"E0");var subQ2=makeQuery(id+"F0.imprint","INTERSECT",VERTEX,{"derivedFrom":[subQ1,subQ0]});Q23=makeQuery(id+"F0.imprint","IMPRINT",FACE,{"disambiguationData":[TD([[makeQuery(id+"F0.imprint","IMPRINT",EDGE,{"disambiguationData":[TD([[subQ2,-1.0]])],"derivedFrom":subQ1}),1.0]])]});}
            var Q24;
            {var subQ0=sQuery(id+"F0.wireOp",EDGE,"E22.2.0");var subQ1=sQuery(id+"F0.wireOp",EDGE,"E0");var subQ2=makeQuery(id+"F0.imprint","INTERSECT",VERTEX,{"derivedFrom":[subQ1,subQ0]});Q24=makeQuery(id+"F0.imprint","IMPRINT",FACE,{"disambiguationData":[TD([[makeQuery(id+"F0.imprint","IMPRINT",EDGE,{"disambiguationData":[TD([[subQ2,-1.0]])],"derivedFrom":subQ1}),1.0]])]});}
            extrude(context, id + "F2", {"entities" : qUnion([Q0, Q1, Q2, Q3, Q4, Q5, Q6, Q7, Q8, Q9, Q10, Q11, Q12, Q13, Q14, Q15, Q16, Q17, Q18, Q19, Q20, Q21, Q22, Q23, Q24]), "operationType" : NewBodyOperationType.ADD, "oppositeDirection" : true, "depth" : 8 * mm});
        }
        {
            var Q0;
            {var subQ5=sQuery(id+"F0.wireOp",EDGE,"E13.MirrorCS");var subQ6=sQuery(id+"F0.wireOp",EDGE,"E0");var subQ7=makeQuery(id+"F0.imprint","INTERSECT",VERTEX,{"derivedFrom":[subQ6,subQ5]});Q0=makeQuery(id+"F0.imprint","IMPRINT",FACE,{"disambiguationData":[TD([[makeQuery(id+"F0.imprint","IMPRINT",EDGE,{"disambiguationData":[TD([[subQ7,-1.0]])],"derivedFrom":subQ6}),1.0]])]});}
            var Q1;
            {var subQ0=sQuery(id+"F0.wireOp",EDGE,"E5.MirrorCS");var subQ1=sQuery(id+"F0.wireOp",EDGE,"E2");var subQ2=makeQuery(id+"F0.imprint","INTERSECT",VERTEX,{"derivedFrom":[subQ1,subQ0]});Q1=makeQuery(id+"F0.imprint","IMPRINT",FACE,{"disambiguationData":[TD([[makeQuery(id+"F0.imprint","IMPRINT",EDGE,{"disambiguationData":[TD([[subQ2,1.0]])],"derivedFrom":subQ1}),1.0]])]});}
            var Q2;
            {var subQ1=sQuery(id+"F0.wireOp",EDGE,"E10");Q2=makeQuery(id+"F0.imprint","IMPRINT",FACE,{"disambiguationData":[TD([[makeQuery(id+"F0.imprint","IMPRINT",EDGE,{"derivedFrom":subQ1}),-1.0]])]});}
            var Q3;
            {var subQ0=sQuery(id+"F0.wireOp",EDGE,"E20.1.3");var subQ1=sQuery(id+"F0.wireOp",EDGE,"E20.1.2");var subQ2=makeQuery(id+"F0.imprint","INTERSECT",VERTEX,{"derivedFrom":[subQ1,subQ0]});Q3=makeQuery(id+"F0.imprint","IMPRINT",FACE,{"disambiguationData":[TD([[makeQuery(id+"F0.imprint","IMPRINT",EDGE,{"disambiguationData":[TD([[subQ2,1.0]])],"derivedFrom":subQ1}),1.0]])]});}
            var Q4;
            {var subQ0=sQuery(id+"F0.wireOp",EDGE,"E21.1.1");Q4=makeQuery(id+"F0.imprint","IMPRINT",FACE,{"disambiguationData":[TD([[makeQuery(id+"F0.imprint","IMPRINT",EDGE,{"derivedFrom":subQ0}),-1.0]])]});}
            var Q5;
            {var subQ6=sQuery(id+"F0.wireOp",EDGE,"E0");var subQ12=sQuery(id+"F0.wireOp",EDGE,"E21.1.3");var subQ13=makeQuery(id+"F0.imprint","INTERSECT",VERTEX,{"derivedFrom":[subQ6,subQ12]});Q5=makeQuery(id+"F0.imprint","IMPRINT",FACE,{"disambiguationData":[TD([[makeQuery(id+"F0.imprint","IMPRINT",EDGE,{"disambiguationData":[TD([[subQ13,-1.0]])],"derivedFrom":subQ6}),1.0]])]});}
            var Q6;
            {var subQ0=sQuery(id+"F0.wireOp",EDGE,"E20.2.3");var subQ1=sQuery(id+"F0.wireOp",EDGE,"E20.2.2");var subQ2=makeQuery(id+"F0.imprint","INTERSECT",VERTEX,{"derivedFrom":[subQ1,subQ0]});Q6=makeQuery(id+"F0.imprint","IMPRINT",FACE,{"disambiguationData":[TD([[makeQuery(id+"F0.imprint","IMPRINT",EDGE,{"disambiguationData":[TD([[subQ2,1.0]])],"derivedFrom":subQ1}),1.0]])]});}
            var Q7;
            {var subQ0=sQuery(id+"F0.wireOp",EDGE,"E21.2.1");Q7=makeQuery(id+"F0.imprint","IMPRINT",FACE,{"disambiguationData":[TD([[makeQuery(id+"F0.imprint","IMPRINT",EDGE,{"derivedFrom":subQ0}),-1.0]])]});}
            var Q8;
            {var subQ9=sQuery(id+"F0.wireOp",EDGE,"E21.2.3");var subQ10=sQuery(id+"F0.wireOp",EDGE,"E0");var subQ11=makeQuery(id+"F0.imprint","INTERSECT",VERTEX,{"derivedFrom":[subQ10,subQ9]});Q8=makeQuery(id+"F0.imprint","IMPRINT",FACE,{"disambiguationData":[TD([[makeQuery(id+"F0.imprint","IMPRINT",EDGE,{"disambiguationData":[TD([[subQ11,-1.0]])],"derivedFrom":subQ10}),1.0]])]});}
            var Q9;
            {var subQ10=sQuery(id+"F0.wireOp",EDGE,"E0");var subQ12=sQuery(id+"F0.wireOp",EDGE,"E21.3.3");var subQ13=makeQuery(id+"F0.imprint","INTERSECT",VERTEX,{"derivedFrom":[subQ10,subQ12]});Q9=makeQuery(id+"F0.imprint","IMPRINT",FACE,{"disambiguationData":[TD([[makeQuery(id+"F0.imprint","IMPRINT",EDGE,{"disambiguationData":[TD([[subQ13,-1.0]])],"derivedFrom":subQ10}),1.0]])]});}
            var Q10;
            {var subQ0=sQuery(id+"F0.wireOp",EDGE,"E21.3.1");Q10=makeQuery(id+"F0.imprint","IMPRINT",FACE,{"disambiguationData":[TD([[makeQuery(id+"F0.imprint","IMPRINT",EDGE,{"derivedFrom":subQ0}),-1.0]])]});}
            var Q11;
            {var subQ0=sQuery(id+"F0.wireOp",EDGE,"E20.3.3");var subQ1=sQuery(id+"F0.wireOp",EDGE,"E20.3.2");var subQ2=makeQuery(id+"F0.imprint","INTERSECT",VERTEX,{"derivedFrom":[subQ1,subQ0]});Q11=makeQuery(id+"F0.imprint","IMPRINT",FACE,{"disambiguationData":[TD([[makeQuery(id+"F0.imprint","IMPRINT",EDGE,{"disambiguationData":[TD([[subQ2,1.0]])],"derivedFrom":subQ1}),1.0]])]});}
            extrude(context, id + "F3", {"entities" : qUnion([Q0, Q1, Q2, Q3, Q4, Q5, Q6, Q7, Q8, Q9, Q10, Q11]), "operationType" : NewBodyOperationType.ADD, "oppositeDirection" : true, "depth" : 4 * mm});
        }
        {
            var Q0;
            {var subQ7=sQuery(id+"F0.wireOp",EDGE,"E5.MirrorCS");var subQ11=sQuery(id+"F0.wireOp",EDGE,"E0");var subQ13=makeQuery(id+"F0.imprint","INTERSECT",VERTEX,{"derivedFrom":[subQ11,subQ7]});Q0=makeQuery(id+"F0.imprint","IMPRINT",FACE,{"disambiguationData":[TD([[makeQuery(id+"F0.imprint","IMPRINT",EDGE,{"disambiguationData":[TD([[subQ13,-1.0]])],"derivedFrom":subQ11}),1.0]])]});}
            var Q1;
            {var subQ0=sQuery(id+"F0.wireOp",EDGE,"E4");var subQ1=sQuery(id+"F0.wireOp",EDGE,"E3.MirrorCS");var subQ2=makeQuery(id+"F0.imprint","INTERSECT",VERTEX,{"derivedFrom":[subQ1,subQ0]});Q1=makeQuery(id+"F0.imprint","IMPRINT",FACE,{"disambiguationData":[TD([[makeQuery(id+"F0.imprint","IMPRINT",EDGE,{"disambiguationData":[TD([[subQ2,1.0]])],"derivedFrom":subQ1}),-1.0]])]});}
            var Q2;
            {var subQ0=sQuery(id+"F0.wireOp",EDGE,"E5.MirrorCS");var subQ1=sQuery(id+"F0.wireOp",EDGE,"E2");var subQ2=makeQuery(id+"F0.imprint","INTERSECT",VERTEX,{"derivedFrom":[subQ1,subQ0]});Q2=makeQuery(id+"F0.imprint","IMPRINT",FACE,{"disambiguationData":[TD([[makeQuery(id+"F0.imprint","IMPRINT",EDGE,{"disambiguationData":[TD([[subQ2,1.0]])],"derivedFrom":subQ1}),1.0]])]});}
            var Q3;
            {var subQ0=sQuery(id+"F0.wireOp",EDGE,"E20.3.1");var subQ1=sQuery(id+"F0.wireOp",EDGE,"E19.MirrorCS");var subQ2=makeQuery(id+"F0.imprint","INTERSECT",VERTEX,{"derivedFrom":[subQ1,subQ0]});Q3=makeQuery(id+"F0.imprint","IMPRINT",FACE,{"disambiguationData":[TD([[makeQuery(id+"F0.imprint","IMPRINT",EDGE,{"disambiguationData":[TD([[subQ2,-1.0]])],"derivedFrom":subQ1}),1.0]])]});}
            var Q4;
            {var subQ0=sQuery(id+"F0.wireOp",EDGE,"E20.3.0");var subQ1=sQuery(id+"F0.wireOp",EDGE,"E0");var subQ2=makeQuery(id+"F0.imprint","INTERSECT",VERTEX,{"derivedFrom":[subQ1,subQ0]});Q4=makeQuery(id+"F0.imprint","IMPRINT",FACE,{"disambiguationData":[TD([[makeQuery(id+"F0.imprint","IMPRINT",EDGE,{"disambiguationData":[TD([[subQ2,1.0]])],"derivedFrom":subQ1}),1.0]])]});}
            var Q5;
            {var subQ0=sQuery(id+"F0.wireOp",EDGE,"E20.3.3");var subQ1=sQuery(id+"F0.wireOp",EDGE,"E20.3.2");var subQ2=makeQuery(id+"F0.imprint","INTERSECT",VERTEX,{"derivedFrom":[subQ1,subQ0]});Q5=makeQuery(id+"F0.imprint","IMPRINT",FACE,{"disambiguationData":[TD([[makeQuery(id+"F0.imprint","IMPRINT",EDGE,{"disambiguationData":[TD([[subQ2,1.0]])],"derivedFrom":subQ1}),1.0]])]});}
            var Q6;
            {var subQ0=sQuery(id+"F0.wireOp",EDGE,"E20.2.1");var subQ1=sQuery(id+"F0.wireOp",EDGE,"E20.2.0");var subQ2=makeQuery(id+"F0.imprint","INTERSECT",VERTEX,{"derivedFrom":[subQ1,subQ0]});Q6=makeQuery(id+"F0.imprint","IMPRINT",FACE,{"disambiguationData":[TD([[makeQuery(id+"F0.imprint","IMPRINT",EDGE,{"disambiguationData":[TD([[subQ2,-1.0]])],"derivedFrom":subQ1}),-1.0]])]});}
            var Q7;
            {var subQ0=sQuery(id+"F0.wireOp",EDGE,"E20.2.3");var subQ1=sQuery(id+"F0.wireOp",EDGE,"E20.2.2");var subQ2=makeQuery(id+"F0.imprint","INTERSECT",VERTEX,{"derivedFrom":[subQ1,subQ0]});Q7=makeQuery(id+"F0.imprint","IMPRINT",FACE,{"disambiguationData":[TD([[makeQuery(id+"F0.imprint","IMPRINT",EDGE,{"disambiguationData":[TD([[subQ2,1.0]])],"derivedFrom":subQ1}),1.0]])]});}
            var Q8;
            {var subQ6=sQuery(id+"F0.wireOp",EDGE,"E0");var subQ11=sQuery(id+"F0.wireOp",EDGE,"E20.2.3");var subQ12=makeQuery(id+"F0.imprint","INTERSECT",VERTEX,{"derivedFrom":[subQ6,subQ11]});Q8=makeQuery(id+"F0.imprint","IMPRINT",FACE,{"disambiguationData":[TD([[makeQuery(id+"F0.imprint","IMPRINT",EDGE,{"disambiguationData":[TD([[subQ12,-1.0]])],"derivedFrom":subQ6}),1.0]])]});}
            var Q9;
            {var subQ0=sQuery(id+"F0.wireOp",EDGE,"E20.1.1");var subQ1=sQuery(id+"F0.wireOp",EDGE,"E20.1.0");var subQ2=makeQuery(id+"F0.imprint","INTERSECT",VERTEX,{"derivedFrom":[subQ1,subQ0]});Q9=makeQuery(id+"F0.imprint","IMPRINT",FACE,{"disambiguationData":[TD([[makeQuery(id+"F0.imprint","IMPRINT",EDGE,{"disambiguationData":[TD([[subQ2,-1.0]])],"derivedFrom":subQ1}),-1.0]])]});}
            var Q10;
            {var subQ6=sQuery(id+"F0.wireOp",EDGE,"E0");var subQ11=sQuery(id+"F0.wireOp",EDGE,"E20.1.3");var subQ13=makeQuery(id+"F0.imprint","INTERSECT",VERTEX,{"derivedFrom":[subQ6,subQ11]});Q10=makeQuery(id+"F0.imprint","IMPRINT",FACE,{"disambiguationData":[TD([[makeQuery(id+"F0.imprint","IMPRINT",EDGE,{"disambiguationData":[TD([[subQ13,-1.0]])],"derivedFrom":subQ6}),1.0]])]});}
            var Q11;
            {var subQ0=sQuery(id+"F0.wireOp",EDGE,"E20.1.3");var subQ1=sQuery(id+"F0.wireOp",EDGE,"E20.1.2");var subQ2=makeQuery(id+"F0.imprint","INTERSECT",VERTEX,{"derivedFrom":[subQ1,subQ0]});Q11=makeQuery(id+"F0.imprint","IMPRINT",FACE,{"disambiguationData":[TD([[makeQuery(id+"F0.imprint","IMPRINT",EDGE,{"disambiguationData":[TD([[subQ2,1.0]])],"derivedFrom":subQ1}),1.0]])]});}
            extrude(context, id + "F4", {"entities" : qUnion([Q0, Q1, Q2, Q3, Q4, Q5, Q6, Q7, Q8, Q9, Q10, Q11]), "operationType" : NewBodyOperationType.REMOVE, "depth" : 4 * mm, "hasSecondDirection" : true, "secondDirectionOppositeDirection" : true, "secondDirectionDepth" : 10 * mm});
        }
        {
            var Q0;
            Q0=makeQuery(id+"F1.opExtrude","CAP_FACE",FACE,{"disambiguationData":[OSD([sQuery(id+"F0.wireOp",EDGE,"E0"),sQuery(id+"F0.wireOp",EDGE,"E23")])],"isStart":false});
            var sketch = newSketch(context, id + "F5", { "sketchPlane" : qUnion([Q0])});
            skLineSegment(sketch, "E24.bottom", {"start": v(28, -28) * mm, "end": v(-28, -28) * mm});
            skLineSegment(sketch, "E24.top", {"start": v(28, 28) * mm, "end": v(-28, 28) * mm});
            skLineSegment(sketch, "E24.left", {"start": v(28, -28) * mm, "end": v(28, 28) * mm});
            skLineSegment(sketch, "E24.right", {"start": v(-28, -28) * mm, "end": v(-28, 28) * mm});
            skPoint(sketch, "E24.middle", {"position": v(0, 0) * mm});
            skLineSegment(sketch, "E25", {"start": v(-18, 28) * mm, "end": v(0, 43) * mm});
            skLineSegment(sketch, "E26.MirrorCS", {"start": v(18, 28) * mm, "end": v(0, 43) * mm});
            skSolve(sketch);
        }
        {
            var Q0;
            Q0=makeQuery(id+"F5.imprint","IMPRINT",FACE,{"disambiguationData":[TD([[makeQuery(id+"F5.imprint","IMPRINT",EDGE,{"derivedFrom":sQuery(id+"F5.wireOp",EDGE,"E24.bottom")}),-1.0]])]});
            var Q1;
            {var subQ0=sQuery(id+"F5.wireOp",EDGE,"E25");Q1=makeQuery(id+"F5.imprint","IMPRINT",FACE,{"disambiguationData":[TD([[makeQuery(id+"F5.imprint","IMPRINT",EDGE,{"derivedFrom":subQ0}),-1.0]])]});}
            extrude(context, id + "F6", {"entities" : qUnion([Q0, Q1]), "operationType" : NewBodyOperationType.REMOVE, "oppositeDirection" : true, "depth" : 6 * mm});
        }
        {
            var Q0;
            Q0=makeQuery(id+"F6.boolean.opBoolean","COPY",EDGE,{"derivedFrom":makeQuery(id+"F6.opExtrude","SWEPT_EDGE",EDGE,{"disambiguationData":[OSD([sQuery(id+"F5.wireOp",EDGE,"E25"),sQuery(id+"F5.wireOp",EDGE,"E26.MirrorCS")])]})});
            var Q1;
            Q1=makeQuery(id+"F6.boolean.opBoolean","COPY",EDGE,{"derivedFrom":makeQuery(id+"F6.opExtrude","SWEPT_EDGE",EDGE,{"disambiguationData":[OSD([sQuery(id+"F5.wireOp",EDGE,"E24.top"),sQuery(id+"F5.wireOp",EDGE,"E25")])]})});
            var Q2;
            Q2=makeQuery(id+"F6.boolean.opBoolean","COPY",EDGE,{"derivedFrom":makeQuery(id+"F6.opExtrude","SWEPT_EDGE",EDGE,{"disambiguationData":[OSD([sQuery(id+"F5.wireOp",EDGE,"E24.top"),sQuery(id+"F5.wireOp",EDGE,"E26.MirrorCS")])]})});
            fillet(context, id + "F7", {"entities" : qUnion([Q0, Q1, Q2]), "radius" : 5 * mm, "tangentPropagation" : true, "allowEdgeOverflow" : false});
        }
        {
            var Q0;
            {var subQ0=sQuery(id+"F0.wireOp",EDGE,"E22.3.1");var subQ1=sQuery(id+"F0.wireOp",EDGE,"E22.1.2");var subQ2=sQuery(id+"F0.wireOp",EDGE,"E22.1.1");var subQ3=sQuery(id+"F0.wireOp",EDGE,"E21.3.0");var subQ4=sQuery(id+"F0.wireOp",EDGE,"E16");var subQ5=sQuery(id+"F0.wireOp",EDGE,"E11.MirrorCS");var subQ6=sQuery(id+"F0.wireOp",EDGE,"E10");var subQ7=sQuery(id+"F0.wireOp",EDGE,"E22.2.3");var subQ8=sQuery(id+"F0.wireOp",EDGE,"E22.2.2");var subQ9=sQuery(id+"F0.wireOp",EDGE,"E22.2.1");var subQ10=sQuery(id+"F0.wireOp",EDGE,"E22.1.3");var subQ11=sQuery(id+"F0.wireOp",EDGE,"E21.3.2");var subQ12=sQuery(id+"F0.wireOp",EDGE,"E21.3.1");var subQ13=sQuery(id+"F0.wireOp",EDGE,"E18.MirrorCS");var subQ14=sQuery(id+"F0.wireOp",EDGE,"E22.3.2");var subQ15=sQuery(id+"F0.wireOp",EDGE,"E23");var subQ16=sQuery(id+"F0.wireOp",EDGE,"E21.1.2");var subQ17=sQuery(id+"F0.wireOp",EDGE,"E21.1.1");var subQ18=sQuery(id+"F0.wireOp",EDGE,"E12");var subQ19=sQuery(id+"F0.wireOp",EDGE,"E22.3.3");var subQ20=sQuery(id+"F0.wireOp",EDGE,"E19.MirrorCS");var subQ21=sQuery(id+"F0.wireOp",EDGE,"E21.1.0");var subQ22=sQuery(id+"F0.wireOp",EDGE,"E21.2.0");var subQ23=sQuery(id+"F0.wireOp",EDGE,"E21.2.2");var subQ24=sQuery(id+"F0.wireOp",EDGE,"E21.2.1");Q0=makeQuery(id+"F4.boolean.opBoolean","SPLIT",FACE,{"disambiguationData":[TD([makeQuery(id+"F1.opExtrude","SWEPT_FACE",FACE,{"disambiguationData":[OSD([subQ15])]})])],"derivedFrom":makeQuery(id+"F2.opExtrude","CAP_FACE",FACE,{"disambiguationData":[OSD([sQuery(id+"F0.wireOp",EDGE,"E0"),subQ6,subQ5,subQ18,subQ4,subQ13,subQ20,subQ21,subQ17,subQ16,subQ22,subQ24,subQ23,subQ3,subQ12,subQ11,subQ2,subQ1,subQ10,subQ9,subQ8,subQ7,subQ0,subQ14,subQ19,subQ15])],"isStart":false})});}
            var sketch = newSketch(context, id + "F8", { "sketchPlane" : qUnion([Q0])});
            skCircle(sketch, "E27", {"center": v(0, 42) * mm, "radius": 2.5 * mm});
            skCircle(sketch, "E28.1.0", {"center": v(-42, 0) * mm, "radius": 2.5 * mm});
            skCircle(sketch, "E28.2.0", {"center": v(0, -42) * mm, "radius": 2.5 * mm});
            skCircle(sketch, "E28.3.0", {"center": v(42, 0) * mm, "radius": 2.5 * mm});
            skPoint(sketch, "E28.center", {"position": v(0, 0) * mm});
            skSolve(sketch);
        }
        {
            var Q0;
            Q0=qSketchRegion(id+"F8",true);
            extrude(context, id + "F9", {"entities" : qUnion([Q0]), "operationType" : NewBodyOperationType.REMOVE, "oppositeDirection" : true, "depth" : 5 * mm});
        }
        {
            var Q0;
            {var subQ5=sQuery(id+"F0.wireOp",EDGE,"E19.MirrorCS");var subQ6=sQuery(id+"F0.wireOp",EDGE,"E0");var subQ7=makeQuery(id+"F0.imprint","INTERSECT",VERTEX,{"derivedFrom":[subQ6,subQ5]});Q0=makeQuery(id+"F0.imprint","IMPRINT",FACE,{"disambiguationData":[TD([[makeQuery(id+"F0.imprint","IMPRINT",EDGE,{"disambiguationData":[TD([[subQ7,-1.0]])],"derivedFrom":subQ6}),1.0]])]});}
            var Q1;
            {var subQ5=sQuery(id+"F0.wireOp",EDGE,"E13.MirrorCS");var subQ6=sQuery(id+"F0.wireOp",EDGE,"E0");var subQ7=makeQuery(id+"F0.imprint","INTERSECT",VERTEX,{"derivedFrom":[subQ6,subQ5]});Q1=makeQuery(id+"F0.imprint","IMPRINT",FACE,{"disambiguationData":[TD([[makeQuery(id+"F0.imprint","IMPRINT",EDGE,{"disambiguationData":[TD([[subQ7,-1.0]])],"derivedFrom":subQ6}),1.0]])]});}
            var Q2;
            {var subQ7=sQuery(id+"F0.wireOp",EDGE,"E5.MirrorCS");var subQ11=sQuery(id+"F0.wireOp",EDGE,"E0");var subQ13=makeQuery(id+"F0.imprint","INTERSECT",VERTEX,{"derivedFrom":[subQ11,subQ7]});Q2=makeQuery(id+"F0.imprint","IMPRINT",FACE,{"disambiguationData":[TD([[makeQuery(id+"F0.imprint","IMPRINT",EDGE,{"disambiguationData":[TD([[subQ13,-1.0]])],"derivedFrom":subQ11}),1.0]])]});}
            var Q3;
            {var subQ3=sQuery(id+"F0.wireOp",EDGE,"E22.1.3");var subQ10=sQuery(id+"F0.wireOp",EDGE,"E0");var subQ11=makeQuery(id+"F0.imprint","INTERSECT",VERTEX,{"derivedFrom":[subQ10,subQ3]});Q3=makeQuery(id+"F0.imprint","IMPRINT",FACE,{"disambiguationData":[TD([[makeQuery(id+"F0.imprint","IMPRINT",EDGE,{"disambiguationData":[TD([[subQ11,-1.0]])],"derivedFrom":subQ10}),1.0]])]});}
            var Q4;
            {var subQ6=sQuery(id+"F0.wireOp",EDGE,"E0");var subQ12=sQuery(id+"F0.wireOp",EDGE,"E21.1.3");var subQ13=makeQuery(id+"F0.imprint","INTERSECT",VERTEX,{"derivedFrom":[subQ6,subQ12]});Q4=makeQuery(id+"F0.imprint","IMPRINT",FACE,{"disambiguationData":[TD([[makeQuery(id+"F0.imprint","IMPRINT",EDGE,{"disambiguationData":[TD([[subQ13,-1.0]])],"derivedFrom":subQ6}),1.0]])]});}
            var Q5;
            {var subQ6=sQuery(id+"F0.wireOp",EDGE,"E0");var subQ11=sQuery(id+"F0.wireOp",EDGE,"E20.1.3");var subQ13=makeQuery(id+"F0.imprint","INTERSECT",VERTEX,{"derivedFrom":[subQ6,subQ11]});Q5=makeQuery(id+"F0.imprint","IMPRINT",FACE,{"disambiguationData":[TD([[makeQuery(id+"F0.imprint","IMPRINT",EDGE,{"disambiguationData":[TD([[subQ13,-1.0]])],"derivedFrom":subQ6}),1.0]])]});}
            var Q6;
            {var subQ3=sQuery(id+"F0.wireOp",EDGE,"E22.2.3");var subQ6=sQuery(id+"F0.wireOp",EDGE,"E0");var subQ14=makeQuery(id+"F0.imprint","INTERSECT",VERTEX,{"derivedFrom":[subQ6,subQ3]});Q6=makeQuery(id+"F0.imprint","IMPRINT",FACE,{"disambiguationData":[TD([[makeQuery(id+"F0.imprint","IMPRINT",EDGE,{"disambiguationData":[TD([[subQ14,-1.0]])],"derivedFrom":subQ6}),1.0]])]});}
            var Q7;
            {var subQ9=sQuery(id+"F0.wireOp",EDGE,"E21.2.3");var subQ10=sQuery(id+"F0.wireOp",EDGE,"E0");var subQ11=makeQuery(id+"F0.imprint","INTERSECT",VERTEX,{"derivedFrom":[subQ10,subQ9]});Q7=makeQuery(id+"F0.imprint","IMPRINT",FACE,{"disambiguationData":[TD([[makeQuery(id+"F0.imprint","IMPRINT",EDGE,{"disambiguationData":[TD([[subQ11,-1.0]])],"derivedFrom":subQ10}),1.0]])]});}
            var Q8;
            {var subQ6=sQuery(id+"F0.wireOp",EDGE,"E0");var subQ11=sQuery(id+"F0.wireOp",EDGE,"E20.2.3");var subQ12=makeQuery(id+"F0.imprint","INTERSECT",VERTEX,{"derivedFrom":[subQ6,subQ11]});Q8=makeQuery(id+"F0.imprint","IMPRINT",FACE,{"disambiguationData":[TD([[makeQuery(id+"F0.imprint","IMPRINT",EDGE,{"disambiguationData":[TD([[subQ12,-1.0]])],"derivedFrom":subQ6}),1.0]])]});}
            var Q9;
            {var subQ3=sQuery(id+"F0.wireOp",EDGE,"E22.3.3");var subQ12=sQuery(id+"F0.wireOp",EDGE,"E0");var subQ13=makeQuery(id+"F0.imprint","INTERSECT",VERTEX,{"derivedFrom":[subQ12,subQ3]});Q9=makeQuery(id+"F0.imprint","IMPRINT",FACE,{"disambiguationData":[TD([[makeQuery(id+"F0.imprint","IMPRINT",EDGE,{"disambiguationData":[TD([[subQ13,-1.0]])],"derivedFrom":subQ12}),1.0]])]});}
            var Q10;
            {var subQ10=sQuery(id+"F0.wireOp",EDGE,"E0");var subQ12=sQuery(id+"F0.wireOp",EDGE,"E21.3.3");var subQ13=makeQuery(id+"F0.imprint","INTERSECT",VERTEX,{"derivedFrom":[subQ10,subQ12]});Q10=makeQuery(id+"F0.imprint","IMPRINT",FACE,{"disambiguationData":[TD([[makeQuery(id+"F0.imprint","IMPRINT",EDGE,{"disambiguationData":[TD([[subQ13,-1.0]])],"derivedFrom":subQ10}),1.0]])]});}
            var Q11;
            {var subQ0=sQuery(id+"F0.wireOp",EDGE,"E20.3.0");var subQ1=sQuery(id+"F0.wireOp",EDGE,"E0");var subQ2=makeQuery(id+"F0.imprint","INTERSECT",VERTEX,{"derivedFrom":[subQ1,subQ0]});Q11=makeQuery(id+"F0.imprint","IMPRINT",FACE,{"disambiguationData":[TD([[makeQuery(id+"F0.imprint","IMPRINT",EDGE,{"disambiguationData":[TD([[subQ2,1.0]])],"derivedFrom":subQ1}),1.0]])]});}
            var Q12;
            {var subQ9=sQuery(id+"F0.wireOp",EDGE,"E10");Q12=makeQuery(id+"F0.imprint","IMPRINT",FACE,{"disambiguationData":[TD([[makeQuery(id+"F0.imprint","IMPRINT",EDGE,{"derivedFrom":subQ9}),1.0]])]});}
            var Q13;
            {var subQ0=sQuery(id+"F0.wireOp",EDGE,"E19.MirrorCS");var subQ1=sQuery(id+"F0.wireOp",EDGE,"E0");var subQ2=makeQuery(id+"F0.imprint","INTERSECT",VERTEX,{"derivedFrom":[subQ1,subQ0]});Q13=makeQuery(id+"F0.imprint","IMPRINT",FACE,{"disambiguationData":[TD([[makeQuery(id+"F0.imprint","IMPRINT",EDGE,{"disambiguationData":[TD([[subQ2,1.0]])],"derivedFrom":subQ1}),1.0]])]});}
            var Q14;
            {var subQ0=sQuery(id+"F0.wireOp",EDGE,"E20.3.1");var subQ1=sQuery(id+"F0.wireOp",EDGE,"E19.MirrorCS");var subQ2=makeQuery(id+"F0.imprint","INTERSECT",VERTEX,{"derivedFrom":[subQ1,subQ0]});Q14=makeQuery(id+"F0.imprint","IMPRINT",FACE,{"disambiguationData":[TD([[makeQuery(id+"F0.imprint","IMPRINT",EDGE,{"disambiguationData":[TD([[subQ2,-1.0]])],"derivedFrom":subQ1}),1.0]])]});}
            var Q15;
            {var subQ1=sQuery(id+"F0.wireOp",EDGE,"E1");var subQ3=sQuery(id+"F0.wireOp",EDGE,"E19.MirrorCS");var subQ4=makeQuery(id+"F0.imprint","INTERSECT",VERTEX,{"derivedFrom":[subQ1,subQ3]});Q15=makeQuery(id+"F0.imprint","IMPRINT",FACE,{"disambiguationData":[TD([[makeQuery(id+"F0.imprint","IMPRINT",EDGE,{"disambiguationData":[TD([[subQ4,-1.0]])],"derivedFrom":subQ3}),-1.0]])]});}
            var Q16;
            {var subQ1=sQuery(id+"F0.wireOp",EDGE,"E1");var subQ3=sQuery(id+"F0.wireOp",EDGE,"E21.3.0");var subQ4=makeQuery(id+"F0.imprint","INTERSECT",VERTEX,{"derivedFrom":[subQ1,subQ3]});Q16=makeQuery(id+"F0.imprint","IMPRINT",FACE,{"disambiguationData":[TD([[makeQuery(id+"F0.imprint","IMPRINT",EDGE,{"disambiguationData":[TD([[subQ4,-1.0]])],"derivedFrom":subQ3}),1.0]])]});}
            var Q17;
            {var subQ0=sQuery(id+"F0.wireOp",EDGE,"E20.3.3");var subQ1=sQuery(id+"F0.wireOp",EDGE,"E20.3.2");var subQ2=makeQuery(id+"F0.imprint","INTERSECT",VERTEX,{"derivedFrom":[subQ1,subQ0]});Q17=makeQuery(id+"F0.imprint","IMPRINT",FACE,{"disambiguationData":[TD([[makeQuery(id+"F0.imprint","IMPRINT",EDGE,{"disambiguationData":[TD([[subQ2,1.0]])],"derivedFrom":subQ1}),1.0]])]});}
            var Q18;
            {var subQ0=sQuery(id+"F0.wireOp",EDGE,"E21.3.0");var subQ1=sQuery(id+"F0.wireOp",EDGE,"E0");var subQ2=makeQuery(id+"F0.imprint","INTERSECT",VERTEX,{"derivedFrom":[subQ1,subQ0]});Q18=makeQuery(id+"F0.imprint","IMPRINT",FACE,{"disambiguationData":[TD([[makeQuery(id+"F0.imprint","IMPRINT",EDGE,{"disambiguationData":[TD([[subQ2,-1.0]])],"derivedFrom":subQ1}),1.0]])]});}
            var Q19;
            {var subQ0=sQuery(id+"F0.wireOp",EDGE,"E22.3.0");var subQ1=sQuery(id+"F0.wireOp",EDGE,"E0");var subQ2=makeQuery(id+"F0.imprint","INTERSECT",VERTEX,{"derivedFrom":[subQ1,subQ0]});Q19=makeQuery(id+"F0.imprint","IMPRINT",FACE,{"disambiguationData":[TD([[makeQuery(id+"F0.imprint","IMPRINT",EDGE,{"disambiguationData":[TD([[subQ2,-1.0]])],"derivedFrom":subQ1}),1.0]])]});}
            var Q20;
            {var subQ0=sQuery(id+"F0.wireOp",EDGE,"E21.3.3");var subQ1=sQuery(id+"F0.wireOp",EDGE,"E1");var subQ2=makeQuery(id+"F0.imprint","INTERSECT",VERTEX,{"derivedFrom":[subQ1,subQ0]});Q20=makeQuery(id+"F0.imprint","IMPRINT",FACE,{"disambiguationData":[TD([[makeQuery(id+"F0.imprint","IMPRINT",EDGE,{"disambiguationData":[TD([[subQ2,-1.0]])],"derivedFrom":subQ1}),-1.0]])]});}
            var Q21;
            {var subQ0=sQuery(id+"F0.wireOp",EDGE,"E20.2.1");var subQ1=sQuery(id+"F0.wireOp",EDGE,"E20.2.0");var subQ2=makeQuery(id+"F0.imprint","INTERSECT",VERTEX,{"derivedFrom":[subQ1,subQ0]});Q21=makeQuery(id+"F0.imprint","IMPRINT",FACE,{"disambiguationData":[TD([[makeQuery(id+"F0.imprint","IMPRINT",EDGE,{"disambiguationData":[TD([[subQ2,-1.0]])],"derivedFrom":subQ1}),-1.0]])]});}
            var Q22;
            {var subQ0=sQuery(id+"F0.wireOp",EDGE,"E20.2.0");var subQ1=sQuery(id+"F0.wireOp",EDGE,"E0");var subQ2=makeQuery(id+"F0.imprint","INTERSECT",VERTEX,{"derivedFrom":[subQ1,subQ0]});Q22=makeQuery(id+"F0.imprint","IMPRINT",FACE,{"disambiguationData":[TD([[makeQuery(id+"F0.imprint","IMPRINT",EDGE,{"disambiguationData":[TD([[subQ2,-1.0]])],"derivedFrom":subQ1}),1.0]])]});}
            var Q23;
            {var subQ1=sQuery(id+"F0.wireOp",EDGE,"E1");var subQ3=sQuery(id+"F0.wireOp",EDGE,"E22.3.3");var subQ4=makeQuery(id+"F0.imprint","INTERSECT",VERTEX,{"derivedFrom":[subQ1,subQ3]});Q23=makeQuery(id+"F0.imprint","IMPRINT",FACE,{"disambiguationData":[TD([[makeQuery(id+"F0.imprint","IMPRINT",EDGE,{"disambiguationData":[TD([[subQ4,-1.0]])],"derivedFrom":subQ3}),-1.0]])]});}
            var Q24;
            {var subQ1=sQuery(id+"F0.wireOp",EDGE,"E1");var subQ3=sQuery(id+"F0.wireOp",EDGE,"E21.2.0");var subQ4=makeQuery(id+"F0.imprint","INTERSECT",VERTEX,{"derivedFrom":[subQ1,subQ3]});Q24=makeQuery(id+"F0.imprint","IMPRINT",FACE,{"disambiguationData":[TD([[makeQuery(id+"F0.imprint","IMPRINT",EDGE,{"disambiguationData":[TD([[subQ4,-1.0]])],"derivedFrom":subQ3}),1.0]])]});}
            var Q25;
            {var subQ0=sQuery(id+"F0.wireOp",EDGE,"E21.2.0");var subQ1=sQuery(id+"F0.wireOp",EDGE,"E0");var subQ2=makeQuery(id+"F0.imprint","INTERSECT",VERTEX,{"derivedFrom":[subQ1,subQ0]});Q25=makeQuery(id+"F0.imprint","IMPRINT",FACE,{"disambiguationData":[TD([[makeQuery(id+"F0.imprint","IMPRINT",EDGE,{"disambiguationData":[TD([[subQ2,-1.0]])],"derivedFrom":subQ1}),1.0]])]});}
            var Q26;
            {var subQ0=sQuery(id+"F0.wireOp",EDGE,"E20.2.3");var subQ1=sQuery(id+"F0.wireOp",EDGE,"E20.2.2");var subQ2=makeQuery(id+"F0.imprint","INTERSECT",VERTEX,{"derivedFrom":[subQ1,subQ0]});Q26=makeQuery(id+"F0.imprint","IMPRINT",FACE,{"disambiguationData":[TD([[makeQuery(id+"F0.imprint","IMPRINT",EDGE,{"disambiguationData":[TD([[subQ2,1.0]])],"derivedFrom":subQ1}),1.0]])]});}
            var Q27;
            {var subQ0=sQuery(id+"F0.wireOp",EDGE,"E22.2.0");var subQ1=sQuery(id+"F0.wireOp",EDGE,"E0");var subQ2=makeQuery(id+"F0.imprint","INTERSECT",VERTEX,{"derivedFrom":[subQ1,subQ0]});Q27=makeQuery(id+"F0.imprint","IMPRINT",FACE,{"disambiguationData":[TD([[makeQuery(id+"F0.imprint","IMPRINT",EDGE,{"disambiguationData":[TD([[subQ2,-1.0]])],"derivedFrom":subQ1}),1.0]])]});}
            var Q28;
            {var subQ0=sQuery(id+"F0.wireOp",EDGE,"E21.2.3");var subQ1=sQuery(id+"F0.wireOp",EDGE,"E1");var subQ2=makeQuery(id+"F0.imprint","INTERSECT",VERTEX,{"derivedFrom":[subQ1,subQ0]});Q28=makeQuery(id+"F0.imprint","IMPRINT",FACE,{"disambiguationData":[TD([[makeQuery(id+"F0.imprint","IMPRINT",EDGE,{"disambiguationData":[TD([[subQ2,-1.0]])],"derivedFrom":subQ1}),-1.0]])]});}
            var Q29;
            {var subQ1=sQuery(id+"F0.wireOp",EDGE,"E1");var subQ3=sQuery(id+"F0.wireOp",EDGE,"E22.2.3");var subQ4=makeQuery(id+"F0.imprint","INTERSECT",VERTEX,{"derivedFrom":[subQ1,subQ3]});Q29=makeQuery(id+"F0.imprint","IMPRINT",FACE,{"disambiguationData":[TD([[makeQuery(id+"F0.imprint","IMPRINT",EDGE,{"disambiguationData":[TD([[subQ4,-1.0]])],"derivedFrom":subQ3}),-1.0]])]});}
            var Q30;
            {var subQ0=sQuery(id+"F0.wireOp",EDGE,"E20.1.1");var subQ1=sQuery(id+"F0.wireOp",EDGE,"E20.1.0");var subQ2=makeQuery(id+"F0.imprint","INTERSECT",VERTEX,{"derivedFrom":[subQ1,subQ0]});Q30=makeQuery(id+"F0.imprint","IMPRINT",FACE,{"disambiguationData":[TD([[makeQuery(id+"F0.imprint","IMPRINT",EDGE,{"disambiguationData":[TD([[subQ2,-1.0]])],"derivedFrom":subQ1}),-1.0]])]});}
            var Q31;
            {var subQ0=sQuery(id+"F0.wireOp",EDGE,"E20.1.0");var subQ1=sQuery(id+"F0.wireOp",EDGE,"E0");var subQ2=makeQuery(id+"F0.imprint","INTERSECT",VERTEX,{"derivedFrom":[subQ1,subQ0]});Q31=makeQuery(id+"F0.imprint","IMPRINT",FACE,{"disambiguationData":[TD([[makeQuery(id+"F0.imprint","IMPRINT",EDGE,{"disambiguationData":[TD([[subQ2,-1.0]])],"derivedFrom":subQ1}),1.0]])]});}
            var Q32;
            {var subQ1=sQuery(id+"F0.wireOp",EDGE,"E1");var subQ3=sQuery(id+"F0.wireOp",EDGE,"E21.1.0");var subQ4=makeQuery(id+"F0.imprint","INTERSECT",VERTEX,{"derivedFrom":[subQ1,subQ3]});Q32=makeQuery(id+"F0.imprint","IMPRINT",FACE,{"disambiguationData":[TD([[makeQuery(id+"F0.imprint","IMPRINT",EDGE,{"disambiguationData":[TD([[subQ4,-1.0]])],"derivedFrom":subQ3}),1.0]])]});}
            var Q33;
            {var subQ0=sQuery(id+"F0.wireOp",EDGE,"E20.1.3");var subQ1=sQuery(id+"F0.wireOp",EDGE,"E20.1.2");var subQ2=makeQuery(id+"F0.imprint","INTERSECT",VERTEX,{"derivedFrom":[subQ1,subQ0]});Q33=makeQuery(id+"F0.imprint","IMPRINT",FACE,{"disambiguationData":[TD([[makeQuery(id+"F0.imprint","IMPRINT",EDGE,{"disambiguationData":[TD([[subQ2,1.0]])],"derivedFrom":subQ1}),1.0]])]});}
            var Q34;
            {var subQ0=sQuery(id+"F0.wireOp",EDGE,"E21.1.0");var subQ1=sQuery(id+"F0.wireOp",EDGE,"E0");var subQ2=makeQuery(id+"F0.imprint","INTERSECT",VERTEX,{"derivedFrom":[subQ1,subQ0]});Q34=makeQuery(id+"F0.imprint","IMPRINT",FACE,{"disambiguationData":[TD([[makeQuery(id+"F0.imprint","IMPRINT",EDGE,{"disambiguationData":[TD([[subQ2,-1.0]])],"derivedFrom":subQ1}),1.0]])]});}
            var Q35;
            {var subQ0=sQuery(id+"F0.wireOp",EDGE,"E21.1.3");var subQ1=sQuery(id+"F0.wireOp",EDGE,"E1");var subQ2=makeQuery(id+"F0.imprint","INTERSECT",VERTEX,{"derivedFrom":[subQ1,subQ0]});Q35=makeQuery(id+"F0.imprint","IMPRINT",FACE,{"disambiguationData":[TD([[makeQuery(id+"F0.imprint","IMPRINT",EDGE,{"disambiguationData":[TD([[subQ2,-1.0]])],"derivedFrom":subQ1}),-1.0]])]});}
            var Q36;
            {var subQ0=sQuery(id+"F0.wireOp",EDGE,"E22.1.0");var subQ1=sQuery(id+"F0.wireOp",EDGE,"E0");var subQ2=makeQuery(id+"F0.imprint","INTERSECT",VERTEX,{"derivedFrom":[subQ1,subQ0]});Q36=makeQuery(id+"F0.imprint","IMPRINT",FACE,{"disambiguationData":[TD([[makeQuery(id+"F0.imprint","IMPRINT",EDGE,{"disambiguationData":[TD([[subQ2,-1.0]])],"derivedFrom":subQ1}),1.0]])]});}
            var Q37;
            {var subQ1=sQuery(id+"F0.wireOp",EDGE,"E1");var subQ3=sQuery(id+"F0.wireOp",EDGE,"E22.1.3");var subQ4=makeQuery(id+"F0.imprint","INTERSECT",VERTEX,{"derivedFrom":[subQ1,subQ3]});Q37=makeQuery(id+"F0.imprint","IMPRINT",FACE,{"disambiguationData":[TD([[makeQuery(id+"F0.imprint","IMPRINT",EDGE,{"disambiguationData":[TD([[subQ4,-1.0]])],"derivedFrom":subQ3}),-1.0]])]});}
            var Q38;
            {var subQ0=sQuery(id+"F0.wireOp",EDGE,"E4");var subQ1=sQuery(id+"F0.wireOp",EDGE,"E3.MirrorCS");var subQ2=makeQuery(id+"F0.imprint","INTERSECT",VERTEX,{"derivedFrom":[subQ1,subQ0]});Q38=makeQuery(id+"F0.imprint","IMPRINT",FACE,{"disambiguationData":[TD([[makeQuery(id+"F0.imprint","IMPRINT",EDGE,{"disambiguationData":[TD([[subQ2,1.0]])],"derivedFrom":subQ1}),-1.0]])]});}
            var Q39;
            {var subQ0=sQuery(id+"F0.wireOp",EDGE,"E4");var subQ1=sQuery(id+"F0.wireOp",EDGE,"E0");var subQ2=makeQuery(id+"F0.imprint","INTERSECT",VERTEX,{"derivedFrom":[subQ1,subQ0]});Q39=makeQuery(id+"F0.imprint","IMPRINT",FACE,{"disambiguationData":[TD([[makeQuery(id+"F0.imprint","IMPRINT",EDGE,{"disambiguationData":[TD([[subQ2,-1.0]])],"derivedFrom":subQ1}),1.0]])]});}
            var Q40;
            {var subQ1=sQuery(id+"F0.wireOp",EDGE,"E1");var subQ3=sQuery(id+"F0.wireOp",EDGE,"E12");var subQ4=makeQuery(id+"F0.imprint","INTERSECT",VERTEX,{"derivedFrom":[subQ1,subQ3]});Q40=makeQuery(id+"F0.imprint","IMPRINT",FACE,{"disambiguationData":[TD([[makeQuery(id+"F0.imprint","IMPRINT",EDGE,{"disambiguationData":[TD([[subQ4,-1.0]])],"derivedFrom":subQ3}),1.0]])]});}
            var Q41;
            {var subQ0=sQuery(id+"F0.wireOp",EDGE,"E5.MirrorCS");var subQ1=sQuery(id+"F0.wireOp",EDGE,"E2");var subQ2=makeQuery(id+"F0.imprint","INTERSECT",VERTEX,{"derivedFrom":[subQ1,subQ0]});Q41=makeQuery(id+"F0.imprint","IMPRINT",FACE,{"disambiguationData":[TD([[makeQuery(id+"F0.imprint","IMPRINT",EDGE,{"disambiguationData":[TD([[subQ2,1.0]])],"derivedFrom":subQ1}),1.0]])]});}
            var Q42;
            {var subQ0=sQuery(id+"F0.wireOp",EDGE,"E12");var subQ1=sQuery(id+"F0.wireOp",EDGE,"E0");var subQ2=makeQuery(id+"F0.imprint","INTERSECT",VERTEX,{"derivedFrom":[subQ1,subQ0]});Q42=makeQuery(id+"F0.imprint","IMPRINT",FACE,{"disambiguationData":[TD([[makeQuery(id+"F0.imprint","IMPRINT",EDGE,{"disambiguationData":[TD([[subQ2,-1.0]])],"derivedFrom":subQ1}),1.0]])]});}
            var Q43;
            {var subQ0=sQuery(id+"F0.wireOp",EDGE,"E13.MirrorCS");var subQ1=sQuery(id+"F0.wireOp",EDGE,"E1");var subQ2=makeQuery(id+"F0.imprint","INTERSECT",VERTEX,{"derivedFrom":[subQ1,subQ0]});Q43=makeQuery(id+"F0.imprint","IMPRINT",FACE,{"disambiguationData":[TD([[makeQuery(id+"F0.imprint","IMPRINT",EDGE,{"disambiguationData":[TD([[subQ2,-1.0]])],"derivedFrom":subQ1}),-1.0]])]});}
            var Q44;
            {var subQ0=sQuery(id+"F0.wireOp",EDGE,"E17");var subQ1=sQuery(id+"F0.wireOp",EDGE,"E0");var subQ2=makeQuery(id+"F0.imprint","INTERSECT",VERTEX,{"derivedFrom":[subQ1,subQ0]});Q44=makeQuery(id+"F0.imprint","IMPRINT",FACE,{"disambiguationData":[TD([[makeQuery(id+"F0.imprint","IMPRINT",EDGE,{"disambiguationData":[TD([[subQ2,-1.0]])],"derivedFrom":subQ1}),1.0]])]});}
            var Q45;
            {var subQ0=sQuery(id+"F0.wireOp",EDGE,"E18.MirrorCS");Q45=makeQuery(id+"F0.imprint","IMPRINT",FACE,{"disambiguationData":[TD([[makeQuery(id+"F0.imprint","IMPRINT",EDGE,{"derivedFrom":subQ0}),1.0]])]});}
            var Q46;
            {var subQ5=sQuery(id+"F0.wireOp",EDGE,"E13.MirrorCS");var subQ7=sQuery(id+"F0.wireOp",EDGE,"E1");var subQ8=makeQuery(id+"F0.imprint","INTERSECT",VERTEX,{"derivedFrom":[subQ7,subQ5]});Q46=makeQuery(id+"F0.imprint","IMPRINT",FACE,{"disambiguationData":[TD([[makeQuery(id+"F0.imprint","IMPRINT",EDGE,{"disambiguationData":[TD([[subQ8,-1.0]])],"derivedFrom":subQ7}),1.0]])]});}
            var Q47;
            {var subQ1=sQuery(id+"F0.wireOp",EDGE,"E10");Q47=makeQuery(id+"F0.imprint","IMPRINT",FACE,{"disambiguationData":[TD([[makeQuery(id+"F0.imprint","IMPRINT",EDGE,{"derivedFrom":subQ1}),-1.0]])]});}
            var Q48;
            {var subQ0=sQuery(id+"F0.wireOp",EDGE,"E22.1.2");Q48=makeQuery(id+"F0.imprint","IMPRINT",FACE,{"disambiguationData":[TD([[makeQuery(id+"F0.imprint","IMPRINT",EDGE,{"derivedFrom":subQ0}),1.0]])]});}
            var Q49;
            {var subQ0=sQuery(id+"F0.wireOp",EDGE,"E21.1.3");var subQ3=sQuery(id+"F0.wireOp",EDGE,"E1");var subQ4=makeQuery(id+"F0.imprint","INTERSECT",VERTEX,{"derivedFrom":[subQ3,subQ0]});Q49=makeQuery(id+"F0.imprint","IMPRINT",FACE,{"disambiguationData":[TD([[makeQuery(id+"F0.imprint","IMPRINT",EDGE,{"disambiguationData":[TD([[subQ4,-1.0]])],"derivedFrom":subQ3}),1.0]])]});}
            var Q50;
            {var subQ0=sQuery(id+"F0.wireOp",EDGE,"E21.1.1");Q50=makeQuery(id+"F0.imprint","IMPRINT",FACE,{"disambiguationData":[TD([[makeQuery(id+"F0.imprint","IMPRINT",EDGE,{"derivedFrom":subQ0}),-1.0]])]});}
            var Q51;
            {var subQ0=sQuery(id+"F0.wireOp",EDGE,"E22.2.2");Q51=makeQuery(id+"F0.imprint","IMPRINT",FACE,{"disambiguationData":[TD([[makeQuery(id+"F0.imprint","IMPRINT",EDGE,{"derivedFrom":subQ0}),1.0]])]});}
            var Q52;
            {var subQ0=sQuery(id+"F0.wireOp",EDGE,"E21.2.3");var subQ3=sQuery(id+"F0.wireOp",EDGE,"E1");var subQ4=makeQuery(id+"F0.imprint","INTERSECT",VERTEX,{"derivedFrom":[subQ3,subQ0]});Q52=makeQuery(id+"F0.imprint","IMPRINT",FACE,{"disambiguationData":[TD([[makeQuery(id+"F0.imprint","IMPRINT",EDGE,{"disambiguationData":[TD([[subQ4,-1.0]])],"derivedFrom":subQ3}),1.0]])]});}
            var Q53;
            {var subQ0=sQuery(id+"F0.wireOp",EDGE,"E21.2.1");Q53=makeQuery(id+"F0.imprint","IMPRINT",FACE,{"disambiguationData":[TD([[makeQuery(id+"F0.imprint","IMPRINT",EDGE,{"derivedFrom":subQ0}),-1.0]])]});}
            var Q54;
            {var subQ0=sQuery(id+"F0.wireOp",EDGE,"E22.3.2");Q54=makeQuery(id+"F0.imprint","IMPRINT",FACE,{"disambiguationData":[TD([[makeQuery(id+"F0.imprint","IMPRINT",EDGE,{"derivedFrom":subQ0}),1.0]])]});}
            var Q55;
            {var subQ0=sQuery(id+"F0.wireOp",EDGE,"E21.3.3");var subQ3=sQuery(id+"F0.wireOp",EDGE,"E1");var subQ4=makeQuery(id+"F0.imprint","INTERSECT",VERTEX,{"derivedFrom":[subQ3,subQ0]});Q55=makeQuery(id+"F0.imprint","IMPRINT",FACE,{"disambiguationData":[TD([[makeQuery(id+"F0.imprint","IMPRINT",EDGE,{"disambiguationData":[TD([[subQ4,-1.0]])],"derivedFrom":subQ3}),1.0]])]});}
            var Q56;
            {var subQ0=sQuery(id+"F0.wireOp",EDGE,"E21.3.1");Q56=makeQuery(id+"F0.imprint","IMPRINT",FACE,{"disambiguationData":[TD([[makeQuery(id+"F0.imprint","IMPRINT",EDGE,{"derivedFrom":subQ0}),-1.0]])]});}
            extrude(context, id + "F10", {"entities" : qUnion([Q0, Q1, Q2, Q3, Q4, Q5, Q6, Q7, Q8, Q9, Q10, Q11, Q12, Q13, Q14, Q15, Q16, Q17, Q18, Q19, Q20, Q21, Q22, Q23, Q24, Q25, Q26, Q27, Q28, Q29, Q30, Q31, Q32, Q33, Q34, Q35, Q36, Q37, Q38, Q39, Q40, Q41, Q42, Q43, Q44, Q45, Q46, Q47, Q48, Q49, Q50, Q51, Q52, Q53, Q54, Q55, Q56]), "offsetDistance" : 25 * mm, "depth" : 2 * mm});
        }
        {
            var Q0;
            Q0=makeQuery(id+"F1.opExtrude","SWEPT_BODY",BODY,{"disambiguationData":[OSD([sQuery(id+"F0.wireOp",EDGE,"E0"),sQuery(id+"F0.wireOp",EDGE,"E23")])]});
            deleteBodies(context, id + "F11", {"entities" : qUnion([Q0])});
        }
        {
            var Q0;
            {var subQ7=sQuery(id+"F0.wireOp",EDGE,"E5.MirrorCS");var subQ11=sQuery(id+"F0.wireOp",EDGE,"E0");var subQ13=makeQuery(id+"F0.imprint","INTERSECT",VERTEX,{"derivedFrom":[subQ11,subQ7]});Q0=makeQuery(id+"F0.imprint","IMPRINT",FACE,{"disambiguationData":[TD([[makeQuery(id+"F0.imprint","IMPRINT",EDGE,{"disambiguationData":[TD([[subQ13,-1.0]])],"derivedFrom":subQ11}),1.0]])]});}
            var Q1;
            {var subQ6=sQuery(id+"F0.wireOp",EDGE,"E0");var subQ11=sQuery(id+"F0.wireOp",EDGE,"E20.1.3");var subQ13=makeQuery(id+"F0.imprint","INTERSECT",VERTEX,{"derivedFrom":[subQ6,subQ11]});Q1=makeQuery(id+"F0.imprint","IMPRINT",FACE,{"disambiguationData":[TD([[makeQuery(id+"F0.imprint","IMPRINT",EDGE,{"disambiguationData":[TD([[subQ13,-1.0]])],"derivedFrom":subQ6}),1.0]])]});}
            var Q2;
            {var subQ6=sQuery(id+"F0.wireOp",EDGE,"E0");var subQ11=sQuery(id+"F0.wireOp",EDGE,"E20.2.3");var subQ12=makeQuery(id+"F0.imprint","INTERSECT",VERTEX,{"derivedFrom":[subQ6,subQ11]});Q2=makeQuery(id+"F0.imprint","IMPRINT",FACE,{"disambiguationData":[TD([[makeQuery(id+"F0.imprint","IMPRINT",EDGE,{"disambiguationData":[TD([[subQ12,-1.0]])],"derivedFrom":subQ6}),1.0]])]});}
            var Q3;
            {var subQ0=sQuery(id+"F0.wireOp",EDGE,"E20.3.0");var subQ1=sQuery(id+"F0.wireOp",EDGE,"E0");var subQ2=makeQuery(id+"F0.imprint","INTERSECT",VERTEX,{"derivedFrom":[subQ1,subQ0]});Q3=makeQuery(id+"F0.imprint","IMPRINT",FACE,{"disambiguationData":[TD([[makeQuery(id+"F0.imprint","IMPRINT",EDGE,{"disambiguationData":[TD([[subQ2,1.0]])],"derivedFrom":subQ1}),1.0]])]});}
            extrude(context, id + "F12", {"entities" : qUnion([Q0, Q1, Q2, Q3]), "operationType" : NewBodyOperationType.ADD, "oppositeDirection" : true, "depth" : 8 * mm});
        }
        {
            var Q0;
            {var subQ6=sQuery(id+"F0.wireOp",EDGE,"E0");var subQ12=sQuery(id+"F0.wireOp",EDGE,"E21.1.3");var subQ13=makeQuery(id+"F0.imprint","INTERSECT",VERTEX,{"derivedFrom":[subQ6,subQ12]});Q0=makeQuery(id+"F0.imprint","IMPRINT",FACE,{"disambiguationData":[TD([[makeQuery(id+"F0.imprint","IMPRINT",EDGE,{"disambiguationData":[TD([[subQ13,-1.0]])],"derivedFrom":subQ6}),1.0]])]});}
            var Q1;
            {var subQ9=sQuery(id+"F0.wireOp",EDGE,"E21.2.3");var subQ10=sQuery(id+"F0.wireOp",EDGE,"E0");var subQ11=makeQuery(id+"F0.imprint","INTERSECT",VERTEX,{"derivedFrom":[subQ10,subQ9]});Q1=makeQuery(id+"F0.imprint","IMPRINT",FACE,{"disambiguationData":[TD([[makeQuery(id+"F0.imprint","IMPRINT",EDGE,{"disambiguationData":[TD([[subQ11,-1.0]])],"derivedFrom":subQ10}),1.0]])]});}
            var Q2;
            {var subQ10=sQuery(id+"F0.wireOp",EDGE,"E0");var subQ12=sQuery(id+"F0.wireOp",EDGE,"E21.3.3");var subQ13=makeQuery(id+"F0.imprint","INTERSECT",VERTEX,{"derivedFrom":[subQ10,subQ12]});Q2=makeQuery(id+"F0.imprint","IMPRINT",FACE,{"disambiguationData":[TD([[makeQuery(id+"F0.imprint","IMPRINT",EDGE,{"disambiguationData":[TD([[subQ13,-1.0]])],"derivedFrom":subQ10}),1.0]])]});}
            var Q3;
            {var subQ5=sQuery(id+"F0.wireOp",EDGE,"E13.MirrorCS");var subQ6=sQuery(id+"F0.wireOp",EDGE,"E0");var subQ7=makeQuery(id+"F0.imprint","INTERSECT",VERTEX,{"derivedFrom":[subQ6,subQ5]});Q3=makeQuery(id+"F0.imprint","IMPRINT",FACE,{"disambiguationData":[TD([[makeQuery(id+"F0.imprint","IMPRINT",EDGE,{"disambiguationData":[TD([[subQ7,-1.0]])],"derivedFrom":subQ6}),1.0]])]});}
            var Q4;
            {var subQ0=sQuery(id+"F0.wireOp",EDGE,"E5.MirrorCS");var subQ1=sQuery(id+"F0.wireOp",EDGE,"E2");var subQ2=makeQuery(id+"F0.imprint","INTERSECT",VERTEX,{"derivedFrom":[subQ1,subQ0]});Q4=makeQuery(id+"F0.imprint","IMPRINT",FACE,{"disambiguationData":[TD([[makeQuery(id+"F0.imprint","IMPRINT",EDGE,{"disambiguationData":[TD([[subQ2,1.0]])],"derivedFrom":subQ1}),1.0]])]});}
            var Q5;
            {var subQ0=sQuery(id+"F0.wireOp",EDGE,"E20.1.3");var subQ1=sQuery(id+"F0.wireOp",EDGE,"E20.1.2");var subQ2=makeQuery(id+"F0.imprint","INTERSECT",VERTEX,{"derivedFrom":[subQ1,subQ0]});Q5=makeQuery(id+"F0.imprint","IMPRINT",FACE,{"disambiguationData":[TD([[makeQuery(id+"F0.imprint","IMPRINT",EDGE,{"disambiguationData":[TD([[subQ2,1.0]])],"derivedFrom":subQ1}),1.0]])]});}
            var Q6;
            {var subQ0=sQuery(id+"F0.wireOp",EDGE,"E20.2.3");var subQ1=sQuery(id+"F0.wireOp",EDGE,"E20.2.2");var subQ2=makeQuery(id+"F0.imprint","INTERSECT",VERTEX,{"derivedFrom":[subQ1,subQ0]});Q6=makeQuery(id+"F0.imprint","IMPRINT",FACE,{"disambiguationData":[TD([[makeQuery(id+"F0.imprint","IMPRINT",EDGE,{"disambiguationData":[TD([[subQ2,1.0]])],"derivedFrom":subQ1}),1.0]])]});}
            var Q7;
            {var subQ0=sQuery(id+"F0.wireOp",EDGE,"E20.3.3");var subQ1=sQuery(id+"F0.wireOp",EDGE,"E20.3.2");var subQ2=makeQuery(id+"F0.imprint","INTERSECT",VERTEX,{"derivedFrom":[subQ1,subQ0]});Q7=makeQuery(id+"F0.imprint","IMPRINT",FACE,{"disambiguationData":[TD([[makeQuery(id+"F0.imprint","IMPRINT",EDGE,{"disambiguationData":[TD([[subQ2,1.0]])],"derivedFrom":subQ1}),1.0]])]});}
            extrude(context, id + "F13", {"entities" : qUnion([Q0, Q1, Q2, Q3, Q4, Q5, Q6, Q7]), "operationType" : NewBodyOperationType.ADD, "oppositeDirection" : true, "depth" : 4 * mm});
        }
        {
            var Q0;
            Q0=makeQuery(id+"F8.imprint","IMPRINT",FACE,{"disambiguationData":[TD([[makeQuery(id+"F8.imprint","IMPRINT",EDGE,{"derivedFrom":sQuery(id+"F8.wireOp",EDGE,"E27")}),1.0]])]});
            var Q1;
            Q1=makeQuery(id+"F8.imprint","IMPRINT",FACE,{"disambiguationData":[TD([[makeQuery(id+"F8.imprint","IMPRINT",EDGE,{"derivedFrom":sQuery(id+"F8.wireOp",EDGE,"E28.3.0")}),1.0]])]});
            var Q2;
            Q2=makeQuery(id+"F8.imprint","IMPRINT",FACE,{"disambiguationData":[TD([[makeQuery(id+"F8.imprint","IMPRINT",EDGE,{"derivedFrom":sQuery(id+"F8.wireOp",EDGE,"E28.2.0")}),1.0]])]});
            var Q3;
            Q3=makeQuery(id+"F8.imprint","IMPRINT",FACE,{"disambiguationData":[TD([[makeQuery(id+"F8.imprint","IMPRINT",EDGE,{"derivedFrom":sQuery(id+"F8.wireOp",EDGE,"E28.1.0")}),1.0]])]});
            extrude(context, id + "F14", {"entities" : qUnion([Q0, Q1, Q2, Q3]), "operationType" : NewBodyOperationType.REMOVE, "oppositeDirection" : true, "depth" : 25 * mm});
        }
        {
            var Q0;
            Q0=makeQuery(id+"F10.opExtrude","CAP_FACE",FACE,{"disambiguationData":[OSD([sQuery(id+"F0.wireOp",EDGE,"E0"),sQuery(id+"F0.wireOp",EDGE,"E23")])],"isStart":false});
            var sketch = newSketch(context, id + "F15", { "sketchPlane" : qUnion([Q0])});
            skText(sketch, "E29", { "text": "12", "fontName": "OpenSans-Regular.ttf"});
            skText(sketch, "E30", { "text": "6", "fontName": "OpenSans-Regular.ttf"});
            skText(sketch, "E31", { "text": "3", "fontName": "OpenSans-Regular.ttf"});
            skText(sketch, "E32", { "text": "9", "fontName": "OpenSans-Regular.ttf"});
            skLineSegment(sketch, "E33", {"start": v(0, 0) * mm, "end": v(30, 51.96) * mm, "construction": true});
            skLineSegment(sketch, "E34", {"start": v(0, 0) * mm, "end": v(51.96, 30) * mm, "construction": true});
            skLineSegment(sketch, "E35.bottom", {"start": v(33.8, 55.54) * mm, "end": v(28.8, 46.88) * mm});
            skLineSegment(sketch, "E35.left", {"start": v(33.8, 55.54) * mm, "end": v(31.2, 57.04) * mm});
            skLineSegment(sketch, "E35.right", {"start": v(28.8, 46.88) * mm, "end": v(26.2, 48.38) * mm});
            skPoint(sketch, "E35.middle", {"position": v(30, 51.96) * mm});
            skLineSegment(sketch, "E36", {"start": v(26.2, 48.38) * mm, "end": v(31.2, 57.04) * mm});
            skLineSegment(sketch, "E37.bottom", {"start": v(57.04, 31.2) * mm, "end": v(48.38, 26.2) * mm});
            skLineSegment(sketch, "E37.top", {"start": v(55.54, 33.8) * mm, "end": v(46.88, 28.8) * mm});
            skLineSegment(sketch, "E37.left", {"start": v(57.04, 31.2) * mm, "end": v(55.54, 33.8) * mm});
            skLineSegment(sketch, "E37.right", {"start": v(48.38, 26.2) * mm, "end": v(46.88, 28.8) * mm});
            skPoint(sketch, "E37.middle", {"position": v(51.96, 30) * mm});
            skLineSegment(sketch, "E38.MirrorCS", {"start": v(0, 0) * mm, "end": v(30, -51.96) * mm, "construction": true});
            skLineSegment(sketch, "E39.MirrorCS", {"start": v(0, 0) * mm, "end": v(51.96, -30) * mm, "construction": true});
            skLineSegment(sketch, "E40.MirrorCS", {"start": v(55.54, -33.8) * mm, "end": v(46.88, -28.8) * mm});
            skLineSegment(sketch, "E41.MirrorCS", {"start": v(57.04, -31.2) * mm, "end": v(48.38, -26.2) * mm});
            skLineSegment(sketch, "E42.MirrorCS", {"start": v(48.38, -26.2) * mm, "end": v(46.88, -28.8) * mm});
            skLineSegment(sketch, "E43.MirrorCS", {"start": v(57.04, -31.2) * mm, "end": v(55.54, -33.8) * mm});
            skLineSegment(sketch, "E44.MirrorCS", {"start": v(28.8, -46.88) * mm, "end": v(26.2, -48.38) * mm});
            skLineSegment(sketch, "E45.MirrorCS", {"start": v(33.8, -55.54) * mm, "end": v(28.8, -46.88) * mm});
            skLineSegment(sketch, "E46.MirrorCS", {"start": v(26.2, -48.38) * mm, "end": v(31.2, -57.04) * mm});
            skLineSegment(sketch, "E47.MirrorCS", {"start": v(33.8, -55.54) * mm, "end": v(31.2, -57.04) * mm});
            skLineSegment(sketch, "E48.MirrorCS", {"start": v(-26.2, 48.38) * mm, "end": v(-31.2, 57.04) * mm});
            skLineSegment(sketch, "E49.MirrorCS", {"start": v(-33.8, 55.54) * mm, "end": v(-31.2, 57.04) * mm});
            skLineSegment(sketch, "E50.MirrorCS", {"start": v(-28.8, 46.88) * mm, "end": v(-26.2, 48.38) * mm});
            skLineSegment(sketch, "E51.MirrorCS", {"start": v(-33.8, 55.54) * mm, "end": v(-28.8, 46.88) * mm});
            skLineSegment(sketch, "E52.MirrorCS", {"start": v(-55.54, 33.8) * mm, "end": v(-46.88, 28.8) * mm});
            skLineSegment(sketch, "E53.MirrorCS", {"start": v(-57.04, 31.2) * mm, "end": v(-48.38, 26.2) * mm});
            skLineSegment(sketch, "E54.MirrorCS", {"start": v(-57.04, 31.2) * mm, "end": v(-55.54, 33.8) * mm});
            skLineSegment(sketch, "E55.MirrorCS", {"start": v(-48.38, 26.2) * mm, "end": v(-46.88, 28.8) * mm});
            skLineSegment(sketch, "E56.MirrorCS", {"start": v(-55.54, -33.8) * mm, "end": v(-46.88, -28.8) * mm});
            skLineSegment(sketch, "E57.MirrorCS", {"start": v(-57.04, -31.2) * mm, "end": v(-55.54, -33.8) * mm});
            skLineSegment(sketch, "E58.MirrorCS", {"start": v(-57.04, -31.2) * mm, "end": v(-48.38, -26.2) * mm});
            skLineSegment(sketch, "E59.MirrorCS", {"start": v(-48.38, -26.2) * mm, "end": v(-46.88, -28.8) * mm});
            skLineSegment(sketch, "E60.MirrorCS", {"start": v(-28.8, -46.88) * mm, "end": v(-26.2, -48.38) * mm});
            skLineSegment(sketch, "E61.MirrorCS", {"start": v(-33.8, -55.54) * mm, "end": v(-31.2, -57.04) * mm});
            skLineSegment(sketch, "E62.MirrorCS", {"start": v(-26.2, -48.38) * mm, "end": v(-31.2, -57.04) * mm});
            skLineSegment(sketch, "E63.MirrorCS", {"start": v(-33.8, -55.54) * mm, "end": v(-28.8, -46.88) * mm});
            const initialGuessF15  = {"E29": [-0.012, 0.05, 1, 0, 0.015], "E30": [-0.00612, -0.065, 1, 0, 0.015], "E31": [0.05, -0.0075, 1, 0, 0.015], "E32": [-0.06215, -0.0075, 1, 0, 0.015]};
            skSetInitialGuess(sketch, initialGuessF15);
            skSolve(sketch);
        }
        {
            var Q0;
            Q0 = qSketchRegion(id + "F15", true);
            extrude(context, id + "F16", {"entities" : qUnion([Q0]), "operationType" : NewBodyOperationType.REMOVE, "oppositeDirection" : true, "offsetDistance" : 25 * mm, "depth" : 1.5 * mm});
        }
        {
            var Q0;
            Q0 = qSketchRegion(id + "F15", true);
            extrude(context, id + "F17", {"entities" : qUnion([Q0]), "oppositeDirection" : true, "depth" : 2 * mm});
        }
        {
            var Q0;
            Q0=makeQuery(id+"F14.boolean.opBoolean","INTERSECT",EDGE,{"derivedFrom":[makeQuery(id+"F10.opExtrude","CAP_FACE",FACE,{"disambiguationData":[OSD([sQuery(id+"F0.wireOp",EDGE,"E0"),sQuery(id+"F0.wireOp",EDGE,"E23")])],"isStart":false}),makeQuery(id+"F14.opExtrude","SWEPT_FACE",FACE,{"disambiguationData":[OSD([sQuery(id+"F8.wireOp",EDGE,"E28.3.0")])]})]});
            var Q1;
            Q1=makeQuery(id+"F14.boolean.opBoolean","INTERSECT",EDGE,{"derivedFrom":[makeQuery(id+"F10.opExtrude","CAP_FACE",FACE,{"disambiguationData":[OSD([sQuery(id+"F0.wireOp",EDGE,"E0"),sQuery(id+"F0.wireOp",EDGE,"E23")])],"isStart":false}),makeQuery(id+"F14.opExtrude","SWEPT_FACE",FACE,{"disambiguationData":[OSD([sQuery(id+"F8.wireOp",EDGE,"E27")])]})]});
            var Q2;
            Q2=makeQuery(id+"F14.boolean.opBoolean","INTERSECT",EDGE,{"derivedFrom":[makeQuery(id+"F10.opExtrude","CAP_FACE",FACE,{"disambiguationData":[OSD([sQuery(id+"F0.wireOp",EDGE,"E0"),sQuery(id+"F0.wireOp",EDGE,"E23")])],"isStart":false}),makeQuery(id+"F14.opExtrude","SWEPT_FACE",FACE,{"disambiguationData":[OSD([sQuery(id+"F8.wireOp",EDGE,"E28.2.0")])]})]});
            var Q3;
            Q3=makeQuery(id+"F14.boolean.opBoolean","INTERSECT",EDGE,{"derivedFrom":[makeQuery(id+"F10.opExtrude","CAP_FACE",FACE,{"disambiguationData":[OSD([sQuery(id+"F0.wireOp",EDGE,"E0"),sQuery(id+"F0.wireOp",EDGE,"E23")])],"isStart":false}),makeQuery(id+"F14.opExtrude","SWEPT_FACE",FACE,{"disambiguationData":[OSD([sQuery(id+"F8.wireOp",EDGE,"E28.1.0")])]})]});
            chamfer(context, id + "F18", {"entities" : qUnion([Q0, Q1, Q2, Q3]), "width" : 2 * mm, "tangentPropagation" : true});
        }
        {
            var Q0;
            {var subQ0=sQuery(id+"F0.wireOp",EDGE,"E0");var subQ1=sQuery(id+"F0.wireOp",EDGE,"E23");Q0=makeQuery(id+"F16.boolean.opBoolean","SPLIT",FACE,{"disambiguationData":[TD([makeQuery(id+"F10.opExtrude","SWEPT_FACE",FACE,{"disambiguationData":[OSD([subQ0])]})])],"derivedFrom":makeQuery(id+"F10.opExtrude","CAP_FACE",FACE,{"disambiguationData":[OSD([subQ0,subQ1])],"isStart":false})});}
            var sketch = newSketch(context, id + "F19", { "sketchPlane" : qUnion([Q0])});
            skText(sketch, "E64", { "text": "Happy", "fontName": "OpenSans-Italic.ttf"});
            skText(sketch, "E65", { "text": "40th", "fontName": "OpenSans-Italic.ttf"});
            skText(sketch, "E66", { "text": "Elise", "fontName": "OpenSans-Italic.ttf"});
            const initialGuessF19  = {"E64": [-0.03495, 0.019, 1, 0, 0.015], "E65": [-0.02622, -0.012, 1, 0, 0.022], "E66": [-0.01469, -0.035, 1, 0, 0.018]};
            skSetInitialGuess(sketch, initialGuessF19);
            skSolve(sketch);
        }
        {
            var Q0;
            Q0 = qSketchRegion(id + "F19", true);
            extrude(context, id + "F20", {"entities" : qUnion([Q0]), "operationType" : NewBodyOperationType.REMOVE, "oppositeDirection" : true, "depth" : 1.5 * mm, "offsetDistance" : 25 * mm});
        }
    });
